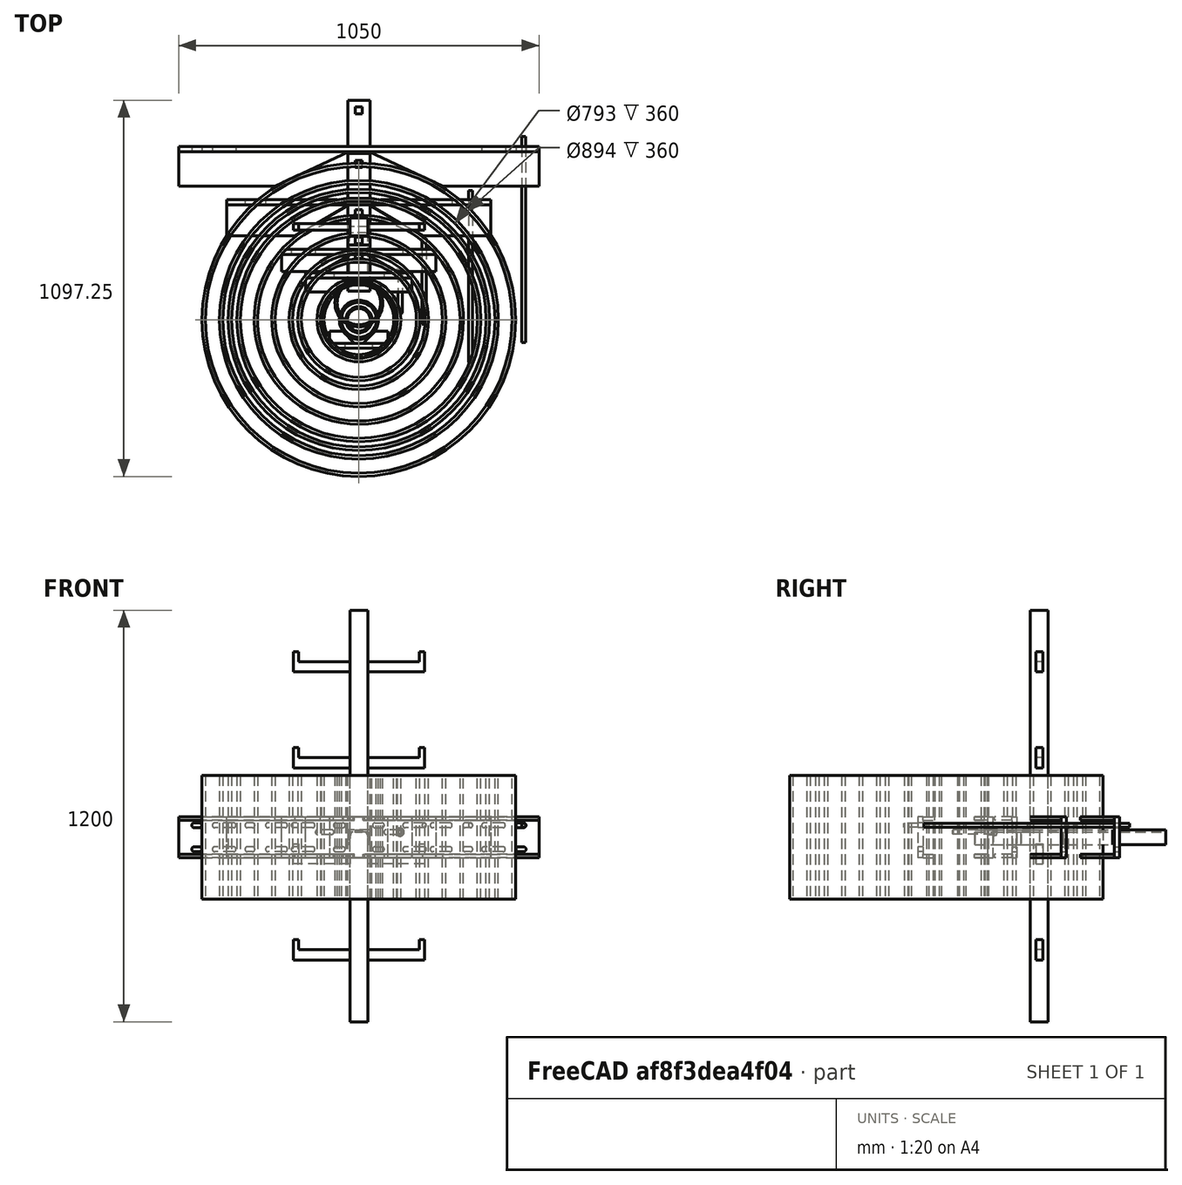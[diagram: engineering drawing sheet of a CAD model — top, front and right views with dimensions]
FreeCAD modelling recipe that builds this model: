
FCSTD DOCUMENT  (FreeCAD 0.21R33694 (Git))
Label: ladder_clamp
License: All rights reserved
LicenseURL: http://en.wikipedia.org/wiki/All_rights_reserved
objects: TechDraw::DrawViewDimension×53, Sketcher::SketchObject×26, Part::Extrusion×25, Part::FeaturePython×17, Part::Feature×15, Part::Cut×12, TechDraw::DrawProjGroupItem×12, App::DocumentObjectGroup×5, TechDraw::DrawSVGTemplate×4, TechDraw::DrawProjGroup×4, TechDraw::DrawViewBalloon×4, TechDraw::DrawViewAnnotation×4, TechDraw::DrawPage×4, Part::Cylinder×3, Fem::ConstraintForce×2, Part::MultiFuse×1, Fem::FemMeshObjectPython×1, Fem::FemSolverObjectPython×1, App::MaterialObjectPython×1, Fem::ConstraintFixed×1, +1 more types
note: 99 computed .brp shape members not serialized (recipe doc carries the construction recipe); baked Part::Feature solids carry a one-line shape summary decoded from their .brp

FEATURE [Part::Feature] BOLTS_part  label="Circular hollow profile 76.1/5.0 l=360.0"
  Placement = pos=(0,0,-120) rot=(0,0,1;0rad)
  shape: bbox 76.1 x 76.1 x 360 mm, 4 faces (baked)
FEATURE [Part::Feature] BOLTS_part001  label="Circular hollow profile 114.3/6.3 l=360.0"
  Placement = pos=(0,0,-120) rot=(0,0,1;0rad)
  shape: bbox 114.3 x 114.3 x 360 mm, 4 faces (baked)
FEATURE [Part::Feature] BOLTS_part002  label="Circular hollow profile 139.7/6.3 l=360.0"
  Placement = pos=(0,49,-120) rot=(0,0,1;0rad)
  shape: bbox 139.7 x 139.7 x 360 mm, 4 faces (baked)
FEATURE [Part::Feature] BOLTS_part003  label="Circular hollow profile 219.1/8.0 l=360.0"
  Placement = pos=(0,0,-120) rot=(0,0,1;0rad)
  shape: bbox 219.1 x 219.1 x 360 mm, 4 faces (baked)
FEATURE [Part::Feature] BOLTS_part004  label="Circular hollow profile 244.5/10.0 l=360.0"
  Placement = pos=(0,0,-120) rot=(0,0,1;0rad)
  shape: bbox 244.5 x 244.5 x 360 mm, 4 faces (baked)
FEATURE [Part::Feature] BOLTS_part005  label="Circular hollow profile 355.6/10.0 l=360.0"
  Placement = pos=(0,0,-120) rot=(0,0,1;0rad)
  shape: bbox 355.6 x 355.6 x 360 mm, 4 faces (baked)
FEATURE [Part::Feature] BOLTS_part006  label="Circular hollow profile 406.4/10.0 l=360.0"
  Placement = pos=(0,0,-120) rot=(0,0,1;0rad)
  shape: bbox 406.4 x 406.4 x 360 mm, 4 faces (baked)
FEATURE [Part::Feature] BOLTS_part007  label="Circular hollow profile 610.0/10.0 l=360.0"
  Placement = pos=(0,0,-120) rot=(0,0,1;0rad)
  shape: bbox 610 x 610 x 360 mm, 4 faces (baked)
FEATURE [Part::Feature] BOLTS_part008  label="Circular hollow profile 914.0/10.0 l=360.0"
  Placement = pos=(0,0,-120) rot=(0,0,1;0rad)
  shape: bbox 914 x 914 x 360 mm, 4 faces (baked)
FEATURE [Sketcher::SketchObject] Sketch
  FullyConstrained = true
  sketch-geometry (10):
    g0: Circle CenterX=0 CenterY=0 CenterZ=0 NormalX=0 NormalY=0 NormalZ=1 AngleXU=0 Radius=57.15
    g1: LineSegment StartX=-47.5 StartY=33.3223 StartZ=0 EndX=-12.5 EndY=68.3223 EndZ=0
    g2: LineSegment StartX=12.5 StartY=68.3223 StartZ=0 EndX=47.5 EndY=33.3223 EndZ=0
    g3: LineSegment StartX=-12.5 StartY=68.3223 StartZ=0 EndX=12.5 EndY=68.3223 EndZ=0
    g4: LineSegment StartX=47.5 StartY=33.3223 StartZ=0 EndX=85 EndY=33.3223 EndZ=0
    g5: LineSegment StartX=85 StartY=33.3223 StartZ=0 EndX=85 EndY=68.3223 EndZ=0
    g6: LineSegment StartX=85 StartY=68.3223 StartZ=0 EndX=12.5 EndY=68.3223 EndZ=0
    g7: LineSegment StartX=-12.5 StartY=68.3223 StartZ=0 EndX=-85 EndY=68.3223 EndZ=0
    g8: LineSegment StartX=-85 StartY=68.3223 StartZ=0 EndX=-85 EndY=33.3223 EndZ=0
    g9: LineSegment StartX=-85 StartY=33.3223 StartZ=0 EndX=-47.5 EndY=33.3223 EndZ=0
  constraints (26):
    c: Coincident(g0,g-1)
    c: Tangent(g1,g0)
    c: Symmetric(g1,g2,g-2)
    c: Symmetric(g1,g2,g-2)
    c: Coincident(g3,g1)
    c: Coincident(g3,g2)
    c: Angle(g-1,g1) = 0.785398
    c: Coincident(g2,g4)
    c: Horizontal(g4)
    c: Coincident(g4,g5)
    c: Vertical(g5)
    c: Coincident(g5,g6)
    c: Coincident(g6,g2)
    c: Horizontal(g6)
    c: Coincident(g1,g7)
    c: Horizontal(g7)
    c: Coincident(g7,g8)
    c: Vertical(g8)
    c: Coincident(g8,g9)
    c: Coincident(g9,g1)
    c: Horizontal(g9)
    c: DistanceY(g5,g5) = 35
    c: Equal(g6,g7)
    c: DistanceX(g6,g6) = 72.5
    c: DistanceX(g7,g5) = 170
    c: Diameter(g0) = 114.3
FEATURE [Part::Extrusion] Extrude  label="Eckblech"
  Base = -> Sketch
  Dir = (0,0,1)
  DirMode = 2
  FaceMakerClass = Part::FaceMakerBullseye
  LengthFwd = 10
  LengthRev = 0
  Solid = true
  Symmetric = false
FEATURE [Part::FeaturePython] Clone  label="Eckblech001"  # Draft clone (typed FeaturePython)
  AttacherType = Attacher::AttachEngine3D
  Fuse = false
  Objects = -> [Extrude]
  Placement = pos=(0,0,110) rot=(0,0,1;0rad)
  Scale = (1,1,1)
FEATURE [Sketcher::SketchObject] Sketch001
  ExternalGeometry = -> [Clone,Extrude]
  FullyConstrained = true
  MapMode = 5
  Placement = pos=(0,68.3223,0) rot=(0,0.707107,0.707107;3.14159rad)
  Support = -> [Extrude]
  sketch-geometry (4):
    g0: LineSegment StartX=-85 StartY=0 StartZ=0 EndX=85 EndY=0 EndZ=0
    g1: LineSegment StartX=85 StartY=0 StartZ=0 EndX=85 EndY=120 EndZ=0
    g2: LineSegment StartX=85 StartY=120 StartZ=0 EndX=-85 EndY=120 EndZ=0
    g3: LineSegment StartX=-85 StartY=120 StartZ=0 EndX=-85 EndY=0 EndZ=0
  constraints (10):
    c: Coincident(g0,g1)
    c: Coincident(g1,g2)
    c: Coincident(g2,g3)
    c: Coincident(g3,g0)
    c: Horizontal(g0)
    c: Horizontal(g2)
    c: Vertical(g1)
    c: Vertical(g3)
    c: Coincident(g0,g-4)
    c: Coincident(g1,g-3)
FEATURE [Part::Extrusion] Extrude001  label="Extrude002"
  Base = -> Sketch001
  Dir = (0,1,-2e-16)
  DirMode = 2
  FaceMakerClass = Part::FaceMakerBullseye
  LengthFwd = 15
  LengthRev = 0
  Solid = true
  Symmetric = false
FEATURE [Sketcher::SketchObject] Sketch002
  ExternalGeometry = -> [Extrude001]
  FullyConstrained = true
  MapMode = 5
  Placement = pos=(0,83.3223,-2e-14) rot=(0,0.707107,0.707107;3.14159rad)
  Support = -> [Extrude001]
  sketch-geometry (13):
    g0: LineSegment StartX=-32.5 StartY=39 StartZ=0 EndX=-32.5 EndY=81 EndZ=0
    g1: LineSegment StartX=-32.5 StartY=81 StartZ=0 EndX=32.5 EndY=81 EndZ=0
    g2: LineSegment StartX=32.5 StartY=81 StartZ=0 EndX=32.5 EndY=39 EndZ=0
    g3: LineSegment StartX=-32.5 StartY=81 StartZ=0 EndX=-85 EndY=120 EndZ=0
    g4: LineSegment StartX=32.5 StartY=81 StartZ=0 EndX=85 EndY=120 EndZ=0
    g5: LineSegment StartX=-16.5 StartY=75.5 StartZ=0 EndX=16.5 EndY=75.5 EndZ=0
    g6: LineSegment StartX=23.89 StartY=69.2796 StartZ=0 EndX=28.5586 EndY=42.3175 EndZ=0
    g7: LineSegment StartX=-23.89 StartY=69.2796 StartZ=0 EndX=-28.5586 EndY=42.3175 EndZ=0
    g8: ArcOfCircle CenterX=32.5 CenterY=43 CenterZ=0 NormalX=0 NormalY=0 NormalZ=1 AngleXU=0 Radius=4 StartAngle=3.31305 EndAngle=4.71239
    g9: ArcOfCircle CenterX=16.5 CenterY=68 CenterZ=0 NormalX=0 NormalY=0 NormalZ=1 AngleXU=0 Radius=7.5 StartAngle=0.171455 EndAngle=1.5708
    g10: ArcOfCircle CenterX=-32.5 CenterY=43 CenterZ=0 NormalX=0 NormalY=0 NormalZ=1 AngleXU=0 Radius=4 StartAngle=4.71239 EndAngle=6.11173
    g11: ArcOfCircle CenterX=-16.5 CenterY=68 CenterZ=0 NormalX=0 NormalY=0 NormalZ=1 AngleXU=0 Radius=7.5 StartAngle=1.5708 EndAngle=2.97014
    g12: LineSegment StartX=-85 StartY=1.42e-14 StartZ=0 EndX=-32.5 EndY=39 EndZ=0
  constraints (35):
    c: Vertical(g0)
    c: Coincident(g0,g1)
    c: Horizontal(g1)
    c: Coincident(g1,g2)
    c: Vertical(g2)
    c: Coincident(g3,g0)
    c: Coincident(g4,g1)
    c: Coincident(g3,g-4)
    c: Coincident(g4,g-3)
    c: Equal(g3,g4)
    c: DistanceX(g1,g1) = 65
    c: DistanceY(g0,g0) = 42
    c: Equal(g0,g2)
    c: PointOnObject(g8,g2)
    c: Coincident(g8,g2)
    c: Coincident(g9,g5)
    c: Vertical(g9,g5)
    c: Tangent(g6,g9) = 1.5708
    c: Tangent(g8,g6) = -1.5708
    c: Symmetric(g5,g5,g-2)
    c: DistanceY(g5,g1) = 5.5
    c: Radius(g9) = 7.5
    c: Radius(g8) = 4
    c: DistanceX(g5,g5) = 33
    c: PointOnObject(g10,g0)
    c: Coincident(g10,g0)
    c: Coincident(g11,g5)
    c: Vertical(g11,g5)
    c: Equal(g9,g11)
    c: Tangent(g11,g7) = -1.5708
    c: Equal(g8,g10)
    c: Tangent(g10,g7) = 1.5708
    c: Coincident(g12,g-4)
    c: Coincident(g12,g0)
    c: Equal(g3,g12)
FEATURE [Part::Extrusion] Extrude002  label="Extrude003"
  Base = -> Sketch002
  Dir = (0,1,-2e-16)
  DirMode = 2
  FaceMakerClass = Part::FaceMakerBullseye
  LengthFwd = 135
  LengthRev = 0
  Solid = true
  Symmetric = false
FEATURE [Sketcher::SketchObject] Sketch003
  ExternalGeometry = -> [Extrude002]
  FullyConstrained = true
  MapMode = 5
  Placement = pos=(0,1.78e-14,81) rot=(0,0,1;0rad)
  Support = -> [Extrude002]
  sketch-geometry (7):
    g0: LineSegment StartX=-10 StartY=198.322 StartZ=0 EndX=10 EndY=198.322 EndZ=0
    g1: LineSegment StartX=10 StartY=198.322 StartZ=0 EndX=10 EndY=178.322 EndZ=0
    g2: LineSegment StartX=10 StartY=178.322 StartZ=0 EndX=-10 EndY=178.322 EndZ=0
    g3: LineSegment StartX=-10 StartY=178.322 StartZ=0 EndX=-10 EndY=198.322 EndZ=0
    g4: LineSegment StartX=-10 StartY=198.322 StartZ=0 EndX=-32.5 EndY=218.322 EndZ=0
    g5: LineSegment StartX=10 StartY=198.322 StartZ=0 EndX=32.5 EndY=218.322 EndZ=0
    g6: LineSegment StartX=10 StartY=188.322 StartZ=0 EndX=32.5 EndY=188.322 EndZ=0
  constraints (19):
    c: Coincident(g0,g1)
    c: Coincident(g1,g2)
    c: Coincident(g2,g3)
    c: Coincident(g3,g0)
    c: Horizontal(g0)
    c: Horizontal(g2)
    c: Vertical(g1)
    c: Vertical(g3)
    c: DistanceX(g2,g2) = 20
    c: DistanceY(g1,g1) = 20
    c: Coincident(g4,g0)
    c: Coincident(g5,g0)
    c: Coincident(g4,g-3)
    c: Coincident(g5,g-3)
    c: Equal(g4,g5)
    c: PointOnObject(g6,g1)
    c: Vertical(g5,g6)
    c: Symmetric(g1,g0,g6)
    c: DistanceY(g6,g5) = 30
FEATURE [Part::Extrusion] Extrude003  label="Extrude004"
  Base = -> Sketch003
  Dir = (0,2e-16,1)
  DirMode = 2
  FaceMakerClass = Part::FaceMakerBullseye
  LengthFwd = 30
  LengthRev = 0
  Solid = true
  Symmetric = true
FEATURE [Part::Cut] Cut  label="U65"
  Base = -> Extrude002
  Refine = true
  Tool = -> Extrude003
FEATURE [Sketcher::SketchObject] Sketch004
  ExternalGeometry = -> [Clone,Extrude]
  FullyConstrained = true
  MapMode = 5
  Placement = pos=(0,68.3223,-1.64e-14) rot=(1,0,0;1.5708rad)
  Support = -> [Extrude001]
  sketch-geometry (19):
    g0: ArcOfCircle CenterX=-67 CenterY=95 CenterZ=0 NormalX=0 NormalY=0 NormalZ=1 AngleXU=0 Radius=7 StartAngle=1.5708 EndAngle=4.71239
    g1: ArcOfCircle CenterX=-47 CenterY=95 CenterZ=0 NormalX=0 NormalY=0 NormalZ=1 AngleXU=0 Radius=7 StartAngle=4.71239 EndAngle=7.85398
    g2: LineSegment StartX=-67 StartY=88 StartZ=0 EndX=-47 EndY=88 EndZ=0
    g3: LineSegment StartX=-67 StartY=102 StartZ=0 EndX=-47 EndY=102 EndZ=0
    g4: ArcOfCircle CenterX=47 CenterY=95 CenterZ=0 NormalX=0 NormalY=0 NormalZ=1 AngleXU=0 Radius=7 StartAngle=1.5708 EndAngle=4.71239
    g5: ArcOfCircle CenterX=67 CenterY=95 CenterZ=0 NormalX=0 NormalY=0 NormalZ=1 AngleXU=0 Radius=7 StartAngle=4.71239 EndAngle=7.85398
    g6: LineSegment StartX=47 StartY=88 StartZ=0 EndX=67 EndY=88 EndZ=0
    g7: LineSegment StartX=47 StartY=102 StartZ=0 EndX=67 EndY=102 EndZ=0
    g8: ArcOfCircle CenterX=-67 CenterY=25 CenterZ=0 NormalX=0 NormalY=0 NormalZ=1 AngleXU=0 Radius=7 StartAngle=1.5708 EndAngle=4.71239
    g9: ArcOfCircle CenterX=-47 CenterY=25 CenterZ=0 NormalX=0 NormalY=0 NormalZ=1 AngleXU=0 Radius=7 StartAngle=4.71239 EndAngle=7.85398
    g10: LineSegment StartX=-67 StartY=18 StartZ=0 EndX=-47 EndY=18 EndZ=0
    g11: LineSegment StartX=-67 StartY=32 StartZ=0 EndX=-47 EndY=32 EndZ=0
    g12: ArcOfCircle CenterX=47 CenterY=25 CenterZ=0 NormalX=0 NormalY=0 NormalZ=1 AngleXU=0 Radius=7 StartAngle=1.5708 EndAngle=4.71239
    g13: ArcOfCircle CenterX=67 CenterY=25 CenterZ=0 NormalX=0 NormalY=0 NormalZ=1 AngleXU=0 Radius=7 StartAngle=4.71239 EndAngle=7.85398
    g14: LineSegment StartX=47 StartY=18 StartZ=0 EndX=67 EndY=18 EndZ=0
    g15: LineSegment StartX=47 StartY=32 StartZ=0 EndX=67 EndY=32 EndZ=0
    g16: LineSegment StartX=-85 StartY=110 StartZ=0 EndX=-67 EndY=95 EndZ=0
    g17: LineSegment StartX=85 StartY=110 StartZ=0 EndX=67 EndY=95 EndZ=0
    g18: LineSegment StartX=-85 StartY=10 StartZ=0 EndX=-67 EndY=25 EndZ=0
  constraints (44):
    c: Tangent(g0,g3) = 1.5708
    c: Tangent(g2,g1) = -1.5708
    c: Tangent(g3,g1) = 1.5708
    c: Equal(g0,g1)
    c: Tangent(g4,g7) = 1.5708
    c: Tangent(g4,g6) = -1.5708
    c: Tangent(g6,g5) = -1.5708
    c: Tangent(g7,g5) = 1.5708
    c: Horizontal(g6)
    c: Equal(g4,g5)
    c: Tangent(g8,g11) = 1.5708
    c: Tangent(g8,g10) = -1.5708
    c: Tangent(g10,g9) = -1.5708
    c: Tangent(g11,g9) = 1.5708
    c: Horizontal(g10)
    c: Equal(g8,g9)
    c: Tangent(g12,g15) = 1.5708
    c: Tangent(g12,g14) = -1.5708
    c: Tangent(g14,g13) = -1.5708
    c: Tangent(g15,g13) = 1.5708
    c: Horizontal(g14)
    c: Equal(g12,g13)
    c: Symmetric(g1,g4,g-2)
    c: Symmetric(g9,g12,g-2)
    c: Vertical(g1,g9)
    c: Equal(g9,g1)
    c: Equal(g1,g4)
    c: Equal(g4,g12)
    c: Equal(g3,g11)
    c: Equal(g11,g7)
    c: Equal(g7,g15)
    c: Diameter(g0) = 14
    c: DistanceX(g3,g3) = 20
    c: Coincident(g16,g-4)
    c: Coincident(g16,g0)
    c: Coincident(g17,g-3)
    c: Coincident(g17,g5)
    c: DistanceY(g8,g0) = 70
    c: Tangent(g0,g2) = -1.5708
    c: DistanceX(g1,g4) = 94
    c: Horizontal(g2)
    c: Coincident(g18,g-6)
    c: Coincident(g18,g8)
    c: Equal(g16,g18)
FEATURE [Part::Extrusion] Extrude004  label="Extrude005"
  Base = -> Sketch004
  Dir = (0,1,0)
  DirMode = 0
  FaceMakerClass = Part::FaceMakerBullseye
  LengthFwd = 50
  LengthRev = 0
  Solid = true
  Symmetric = true
FEATURE [Part::Cut] Cut001
  Base = -> Extrude001
  Refine = true
  Tool = -> Extrude004
FEATURE [Part::FeaturePython] BooleanFragments  # WARN: FeaturePython — macro-defined, semantics opaque (R4)
  Mode = 0
  Objects = -> [Extrude,Clone,Cut001]
  Tolerance = 0
FEATURE [Part::FeaturePython] Clone001  label="BooleanFragments001"  # Draft clone (typed FeaturePython)
  AttacherType = Attacher::AttachEngine3D
  Fuse = false
  Objects = -> [BooleanFragments]
  Placement = pos=(0,0,0) rot=(0,0,1;3.14159rad)
  Scale = (1,1,1)
FEATURE [Sketcher::SketchObject] Sketch005  label="Basis"
  FullyConstrained = true
  sketch-geometry (10):
    g0: Circle CenterX=0 CenterY=0 CenterZ=0 NormalX=0 NormalY=0 NormalZ=1 AngleXU=0 Radius=57.15
    g1: LineSegment StartX=-47.5 StartY=33.3223 StartZ=0 EndX=-12.5 EndY=68.3223 EndZ=0
    g2: LineSegment StartX=12.5 StartY=68.3223 StartZ=0 EndX=47.5 EndY=33.3223 EndZ=0
    g3: LineSegment StartX=-12.5 StartY=68.3223 StartZ=0 EndX=12.5 EndY=68.3223 EndZ=0
    g4: LineSegment StartX=47.5 StartY=33.3223 StartZ=0 EndX=85 EndY=33.3223 EndZ=0
    g5: LineSegment StartX=85 StartY=33.3223 StartZ=0 EndX=85 EndY=68.3223 EndZ=0
    g6: LineSegment StartX=85 StartY=68.3223 StartZ=0 EndX=12.5 EndY=68.3223 EndZ=0
    g7: LineSegment StartX=-12.5 StartY=68.3223 StartZ=0 EndX=-85 EndY=68.3223 EndZ=0
    g8: LineSegment StartX=-85 StartY=68.3223 StartZ=0 EndX=-85 EndY=33.3223 EndZ=0
    g9: LineSegment StartX=-85 StartY=33.3223 StartZ=0 EndX=-47.5 EndY=33.3223 EndZ=0
  constraints (26):
    c: Coincident(g0,g-1)
    c: Tangent(g1,g0)
    c: Symmetric(g1,g2,g-2)
    c: Symmetric(g1,g2,g-2)
    c: Coincident(g3,g1)
    c: Coincident(g3,g2)
    c: Angle(g-1,g1) = 0.785398
    c: Coincident(g2,g4)
    c: Horizontal(g4)
    c: Coincident(g4,g5)
    c: Vertical(g5)
    c: Coincident(g5,g6)
    c: Coincident(g6,g2)
    c: Horizontal(g6)
    c: Coincident(g1,g7)
    c: Horizontal(g7)
    c: Coincident(g7,g8)
    c: Vertical(g8)
    c: Coincident(g8,g9)
    c: Coincident(g9,g1)
    c: Horizontal(g9)
    c: DistanceY(g5,g5) = 35
    c: Equal(g6,g7)
    c: DistanceX(g6,g6) = 72.5
    c: DistanceX(g7,g5) = 170
    c: Diameter(g0) = 114.3
FEATURE [App::DocumentObjectGroup] Group001  label="R76_114"
  Group = -> [Cut,BooleanFragments,Clone001,BOLTS_part,BOLTS_part001,Sketch005]
FEATURE [TechDraw::DrawSVGTemplate] Template
  EditableTexts = AUTHOR_NAME=Thomas Schrader,DN=1,DRAWING_TITLE=Leiterhalterung,FC-DATE=06.05.2021,FC-SC=1:2,FC-SH=X / Y,FC-SI=A3,FreeCAD_DRAWING=Material: Stahl S235,+5 more (map truncated)
  Height = 297
  Orientation = 1
  Width = 420
FEATURE [TechDraw::DrawProjGroupItem] ProjItem  label="Front"
  CoarseView = false
  Direction = (0,1,0)
  Focus = 100
  HardHidden = false
  IsoCount = 0
  IsoHidden = false
  IsoVisible = false
  LockPosition = true
  Perspective = false
  Rotation = 0
  RotationVector = (-1,0,0)
  Scale = 0.5
  ScaleType = 2
  ScrubCount = 0
  SeamHidden = false
  SeamVisible = true
  SmoothHidden = false
  SmoothVisible = true
  Source = -> [Cut,BooleanFragments]
  Type = 0
  X = 0
  XDirection = (-1,0,0)
  Y = 0
FEATURE [TechDraw::DrawProjGroupItem] ProjItem001  label="Left"
  CoarseView = false
  Direction = (1,1e-16,0)
  Focus = 100
  HardHidden = true
  IsoCount = 0
  IsoHidden = false
  IsoVisible = false
  LockPosition = false
  Perspective = false
  Rotation = 0
  RotationVector = (1,0,0)
  Scale = 0.2
  ScaleType = 2
  ScrubCount = 0
  SeamHidden = false
  SeamVisible = true
  SmoothHidden = false
  SmoothVisible = true
  Source = -> [Cut,BooleanFragments]
  Type = 1
  X = 103.75
  XDirection = (-1e-16,1,0)
  Y = 0
FEATURE [TechDraw::DrawProjGroupItem] ProjItem002  label="Top"
  CoarseView = false
  Direction = (0,0,1)
  Focus = 100
  HardHidden = true
  IsoCount = 0
  IsoHidden = false
  IsoVisible = false
  LockPosition = false
  Perspective = false
  Rotation = 0
  RotationVector = (1,0,0)
  Scale = 0.2
  ScaleType = 2
  ScrubCount = 0
  SeamHidden = false
  SeamVisible = true
  SmoothHidden = false
  SmoothVisible = true
  Source = -> [Cut,BooleanFragments]
  Type = 4
  X = 0
  XDirection = (-1,0,0)
  Y = -91.25
FEATURE [TechDraw::DrawProjGroup] ProjGroup
  Anchor = -> ProjItem
  AutoDistribute = true
  LockPosition = false
  ProjectionType = 0
  Rotation = 0
  Scale = 0.5
  ScaleType = 2
  Source = -> [Cut,BooleanFragments]
  Views = -> [ProjItem,ProjItem001,ProjItem002]
  X = 116.09
  Y = 219.887
  spacingX = 15
  spacingY = 15
FEATURE [TechDraw::DrawViewDimension] Dimension
  AngleOverride = false
  Arbitrary = false
  ArbitraryTolerances = false
  EqualTolerance = true
  ExtensionAngle = 0
  FormatSpec = %.1f
  FormatSpecOverTolerance = %+.1f
  FormatSpecUnderTolerance = %+.1f
  Inverted = false
  LineAngle = 0
  LockPosition = false
  MeasureType = 1
  OverTolerance = 0
  References2D = -> [ProjItem002]
  Rotation = 0
  Scale = 0.2
  ScaleType = 2
  TheoreticalExact = false
  Type = 2
  UnderTolerance = 0
  X = -71.0566
  Y = 37.5
FEATURE [TechDraw::DrawViewDimension] Dimension001
  AngleOverride = false
  Arbitrary = false
  ArbitraryTolerances = false
  EqualTolerance = true
  ExtensionAngle = 0
  FormatSpec = %.1f
  FormatSpecOverTolerance = %+.1f
  FormatSpecUnderTolerance = %+.1f
  Inverted = false
  LineAngle = 0
  LockPosition = false
  MeasureType = 1
  OverTolerance = 0
  References2D = -> [ProjItem002]
  Rotation = 0
  Scale = 0.2
  ScaleType = 2
  TheoreticalExact = false
  Type = 2
  UnderTolerance = 0
  X = -64.7644
  Y = 11.2057
FEATURE [TechDraw::DrawViewDimension] Dimension002
  AngleOverride = false
  Arbitrary = false
  ArbitraryTolerances = false
  EqualTolerance = true
  ExtensionAngle = 0
  FormatSpec = %.1f
  FormatSpecOverTolerance = %+.1f
  FormatSpecUnderTolerance = %+.1f
  Inverted = false
  LineAngle = 0
  LockPosition = false
  MeasureType = 1
  OverTolerance = 0
  References2D = -> [ProjItem]
  Rotation = 0
  Scale = 0.2
  ScaleType = 2
  TheoreticalExact = false
  Type = 1
  UnderTolerance = 0
  X = -0.318123
  Y = 46.2243
FEATURE [TechDraw::DrawViewDimension] Dimension003
  AngleOverride = false
  Arbitrary = false
  ArbitraryTolerances = false
  EqualTolerance = true
  ExtensionAngle = 0
  FormatSpec = %.1f
  FormatSpecOverTolerance = %+.1f
  FormatSpecUnderTolerance = %+.1f
  Inverted = false
  LineAngle = 0
  LockPosition = false
  MeasureType = 1
  OverTolerance = 0
  References2D = -> [ProjItem]
  Rotation = 0
  Scale = 0.2
  ScaleType = 2
  TheoreticalExact = false
  Type = 2
  UnderTolerance = 0
  X = -71.4492
  Y = 0.95437
FEATURE [TechDraw::DrawViewDimension] Dimension004
  AngleOverride = false
  Arbitrary = false
  ArbitraryTolerances = false
  EqualTolerance = true
  ExtensionAngle = 0
  FormatSpec = ⌀%.1f
  FormatSpecOverTolerance = %+.1f
  FormatSpecUnderTolerance = %+.1f
  Inverted = false
  LineAngle = 0
  LockPosition = false
  MeasureType = 1
  OverTolerance = 0
  References2D = -> [ProjItem]
  Rotation = 0
  Scale = 0.2
  ScaleType = 2
  TheoreticalExact = false
  Type = 5
  UnderTolerance = 0
  X = 49.0059
  Y = 14.3186
FEATURE [TechDraw::DrawViewDimension] Dimension005
  AngleOverride = false
  Arbitrary = false
  ArbitraryTolerances = false
  EqualTolerance = true
  ExtensionAngle = 0
  FormatSpec = %.1f
  FormatSpecOverTolerance = %+.1f
  FormatSpecUnderTolerance = %+.1f
  Inverted = false
  LineAngle = 0
  LockPosition = false
  MeasureType = 1
  OverTolerance = 0
  References2D = -> [ProjItem]
  Rotation = 0
  Scale = 0.2
  ScaleType = 2
  TheoreticalExact = false
  Type = 1
  UnderTolerance = 0
  X = -28.5
  Y = 7.01313
FEATURE [TechDraw::DrawViewDimension] Dimension006
  AngleOverride = false
  Arbitrary = false
  ArbitraryTolerances = false
  EqualTolerance = true
  ExtensionAngle = 0
  FormatSpec = %.1f
  FormatSpecOverTolerance = %+.1f
  FormatSpecUnderTolerance = %+.1f
  Inverted = false
  LineAngle = 0
  LockPosition = false
  MeasureType = 1
  OverTolerance = 0
  References2D = -> [ProjItem]
  Rotation = 0
  Scale = 0.2
  ScaleType = 2
  TheoreticalExact = false
  Type = 2
  UnderTolerance = 0
  X = -54.6754
  Y = 3.4284
FEATURE [TechDraw::DrawViewDimension] Dimension007
  AngleOverride = false
  Arbitrary = false
  ArbitraryTolerances = false
  EqualTolerance = true
  ExtensionAngle = 0
  FormatSpec = %.1f
  FormatSpecOverTolerance = %+.1f
  FormatSpecUnderTolerance = %+.1f
  Inverted = false
  LineAngle = 0
  LockPosition = false
  MeasureType = 1
  OverTolerance = 0
  References2D = -> [ProjItem]
  Rotation = 0
  Scale = 0.2
  ScaleType = 2
  TheoreticalExact = false
  Type = 1
  UnderTolerance = 0
  X = -0.403341
  Y = -37.2637
FEATURE [TechDraw::DrawViewDimension] Dimension008
  AngleOverride = false
  Arbitrary = false
  ArbitraryTolerances = false
  EqualTolerance = true
  ExtensionAngle = 0
  FormatSpec = %.1f
  FormatSpecOverTolerance = %+.1f
  FormatSpecUnderTolerance = %+.1f
  Inverted = false
  LineAngle = 0
  LockPosition = false
  MeasureType = 1
  OverTolerance = 0
  References2D = -> [ProjItem002]
  Rotation = 0
  Scale = 0.2
  ScaleType = 2
  TheoreticalExact = false
  Type = 1
  UnderTolerance = 0
  X = 32.8723
  Y = -34.6868
FEATURE [TechDraw::DrawViewDimension] Dimension009
  AngleOverride = false
  Arbitrary = false
  ArbitraryTolerances = false
  EqualTolerance = true
  ExtensionAngle = 0
  FormatSpec = %.1f
  FormatSpecOverTolerance = %+.1f
  FormatSpecUnderTolerance = %+.1f
  Inverted = false
  LineAngle = 0
  LockPosition = false
  MeasureType = 1
  OverTolerance = 0
  References2D = -> [ProjItem002]
  Rotation = 0
  Scale = 0.2
  ScaleType = 2
  TheoreticalExact = false
  Type = 2
  UnderTolerance = 0
  X = 19.5011
  Y = -16.5424
FEATURE [TechDraw::DrawViewDimension] Dimension010
  AngleOverride = false
  Arbitrary = false
  ArbitraryTolerances = false
  EqualTolerance = true
  ExtensionAngle = 0
  FormatSpec = %.1f
  FormatSpecOverTolerance = %+.1f
  FormatSpecUnderTolerance = %+.1f
  Inverted = false
  LineAngle = 0
  LockPosition = false
  MeasureType = 1
  OverTolerance = 0
  References2D = -> [ProjItem002]
  Rotation = 0
  Scale = 0.2
  ScaleType = 2
  TheoreticalExact = false
  Type = 2
  UnderTolerance = 0
  X = -50.5722
  Y = 0.025058
FEATURE [TechDraw::DrawViewDimension] Dimension011
  AngleOverride = false
  Arbitrary = false
  ArbitraryTolerances = false
  EqualTolerance = true
  ExtensionAngle = 0
  FormatSpec = %.1f
  FormatSpecOverTolerance = %+.1f
  FormatSpecUnderTolerance = %+.1f
  Inverted = false
  LineAngle = 0
  LockPosition = false
  MeasureType = 1
  OverTolerance = 0
  References2D = -> [ProjItem001]
  Rotation = 0
  Scale = 0.2
  ScaleType = 2
  TheoreticalExact = false
  Type = 1
  UnderTolerance = 0
  X = 12.5684
  Y = 23.4751
FEATURE [TechDraw::DrawViewBalloon] Balloon
  BubbleShape = 0
  EndType = 0
  EndTypeScale = 1
  KinkLength = 5
  LockPosition = false
  OriginX = 82.506
  OriginY = -1.18058
  Rotation = 0
  Scale = 0.2
  ScaleType = 2
  ShapeScale = 1
  SourceView = -> ProjItem001
  Text = 1
  TextWrapLen = -1
  X = 122.506
  Y = 38.8194
FEATURE [TechDraw::DrawViewAnnotation] Annotation
  Font = Arial
  LineSpace = 80
  LockPosition = false
  MaxWidth = -1
  Rotation = 0
  Scale = 0.2
  ScaleType = 2
  Text = U-65
  TextSize = 5
  TextStyle = 0
  X = 299.213
  Y = 237.713
FEATURE [TechDraw::DrawPage] Page  label="Page_R76_R114"
  KeepUpdated = true
  NextBalloonIndex = 2
  ProjectionType = 0
  Template = -> Template
  Views = -> [ProjGroup,Dimension,Dimension001,Dimension002,Dimension003,Dimension004,Dimension005,Dimension006,Dimension007,Dimension008,Dimension009,Dimension010,Dimension011,Balloon,Annotation]
FEATURE [Sketcher::SketchObject] Sketch007
  FullyConstrained = true
  sketch-geometry (10):
    g0: Circle CenterX=0 CenterY=0 CenterZ=0 NormalX=0 NormalY=0 NormalZ=1 AngleXU=0 Radius=109.55
    g1: LineSegment StartX=-74.6259 StartY=81.4822 StartZ=0 EndX=-17.5 EndY=121.482 EndZ=0
    g2: LineSegment StartX=17.5 StartY=121.482 StartZ=0 EndX=74.6259 EndY=81.4822 EndZ=0
    g3: LineSegment StartX=-17.5 StartY=121.482 StartZ=0 EndX=17.5 EndY=121.482 EndZ=0
    g4: LineSegment StartX=74.6259 StartY=81.4822 StartZ=0 EndX=155 EndY=81.4822 EndZ=0
    g5: LineSegment StartX=155 StartY=81.4822 StartZ=0 EndX=155 EndY=121.482 EndZ=0
    g6: LineSegment StartX=155 StartY=121.482 StartZ=0 EndX=17.5 EndY=121.482 EndZ=0
    g7: LineSegment StartX=-17.5 StartY=121.482 StartZ=0 EndX=-155 EndY=121.482 EndZ=0
    g8: LineSegment StartX=-155 StartY=121.482 StartZ=0 EndX=-155 EndY=81.4822 EndZ=0
    g9: LineSegment StartX=-155 StartY=81.4822 StartZ=0 EndX=-74.6259 EndY=81.4822 EndZ=0
  constraints (26):
    c: Coincident(g0,g-1)
    c: Tangent(g1,g0)
    c: Symmetric(g1,g2,g-2)
    c: Symmetric(g1,g2,g-2)
    c: Coincident(g3,g1)
    c: Coincident(g3,g2)
    c: Coincident(g2,g4)
    c: Horizontal(g4)
    c: Coincident(g4,g5)
    c: Vertical(g5)
    c: Coincident(g5,g6)
    c: Coincident(g6,g2)
    c: Horizontal(g6)
    c: Coincident(g1,g7)
    c: Horizontal(g7)
    c: Coincident(g7,g8)
    c: Vertical(g8)
    c: Coincident(g8,g9)
    c: Coincident(g9,g1)
    c: Horizontal(g9)
    c: DistanceY(g5,g5) = 40
    c: Equal(g6,g7)
    c: Diameter(g0) = 219.1
    c: DistanceX(g1,g2) = 35
    c: Angle(g-1,g1) = 0.610865
    c: DistanceX(g7,g5) = 310
FEATURE [Part::Extrusion] Extrude005  label="Eckblech002"
  Base = -> Sketch007
  Dir = (0,0,1)
  DirMode = 2
  FaceMakerClass = Part::FaceMakerBullseye
  LengthFwd = 10
  LengthRev = 0
  Solid = true
  Symmetric = false
FEATURE [Part::FeaturePython] Clone004  label="Eckblech003"  # Draft clone (typed FeaturePython)
  AttacherType = Attacher::AttachEngine3D
  Fuse = false
  Objects = -> [Extrude005]
  Placement = pos=(0,0,110) rot=(0,0,1;0rad)
  Scale = (1,1,1)
FEATURE [Sketcher::SketchObject] Sketch008
  ExternalGeometry = -> [Clone004,Extrude005]
  FullyConstrained = true
  MapMode = 5
  Placement = pos=(0,121.482,0) rot=(0,0.707107,0.707107;3.14159rad)
  Support = -> [Extrude005]
  sketch-geometry (4):
    g0: LineSegment StartX=-155 StartY=0 StartZ=0 EndX=155 EndY=0 EndZ=0
    g1: LineSegment StartX=155 StartY=0 StartZ=0 EndX=155 EndY=120 EndZ=0
    g2: LineSegment StartX=155 StartY=120 StartZ=0 EndX=-155 EndY=120 EndZ=0
    g3: LineSegment StartX=-155 StartY=120 StartZ=0 EndX=-155 EndY=0 EndZ=0
  constraints (10):
    c: Coincident(g0,g1)
    c: Coincident(g1,g2)
    c: Coincident(g2,g3)
    c: Coincident(g3,g0)
    c: Horizontal(g0)
    c: Horizontal(g2)
    c: Vertical(g1)
    c: Vertical(g3)
    c: Coincident(g0,g-4)
    c: Coincident(g1,g-3)
FEATURE [Part::Extrusion] Extrude006
  Base = -> Sketch008
  Dir = (0,1,-2e-16)
  DirMode = 2
  FaceMakerClass = Part::FaceMakerBullseye
  LengthFwd = 15
  LengthRev = 0
  Solid = true
  Symmetric = false
FEATURE [Sketcher::SketchObject] Sketch009
  ExternalGeometry = -> [Extrude006]
  FullyConstrained = true
  MapMode = 5
  Placement = pos=(0,136.482,-3.28e-14) rot=(0,0.707107,0.707107;3.14159rad)
  Support = -> [Extrude006]
  sketch-geometry (11):
    g0: LineSegment StartX=-32.5 StartY=39 StartZ=0 EndX=-32.5 EndY=81 EndZ=0
    g1: LineSegment StartX=-32.5 StartY=81 StartZ=0 EndX=32.5 EndY=81 EndZ=0
    g2: LineSegment StartX=32.5 StartY=81 StartZ=0 EndX=32.5 EndY=39 EndZ=0
    g3: LineSegment StartX=-32.5 StartY=81 StartZ=0 EndX=-155 EndY=120 EndZ=0
    g4: LineSegment StartX=32.5 StartY=81 StartZ=0 EndX=155 EndY=120 EndZ=0
    g5: LineSegment StartX=-26.5 StartY=75.5 StartZ=0 EndX=26.5 EndY=75.5 EndZ=0
    g6: LineSegment StartX=26.5 StartY=75.5 StartZ=0 EndX=26.5 EndY=39 EndZ=0
    g7: LineSegment StartX=-26.5 StartY=75.5 StartZ=0 EndX=-26.5 EndY=39 EndZ=0
    g8: LineSegment StartX=-155 StartY=2.84e-14 StartZ=0 EndX=-32.5 EndY=39 EndZ=0
    g9: LineSegment StartX=-32.5 StartY=39 StartZ=0 EndX=-26.5 EndY=39 EndZ=0
    g10: LineSegment StartX=26.5 StartY=39 StartZ=0 EndX=32.5 EndY=39 EndZ=0
  constraints (29):
    c: Vertical(g0)
    c: Coincident(g0,g1)
    c: Horizontal(g1)
    c: Coincident(g1,g2)
    c: Vertical(g2)
    c: Coincident(g3,g0)
    c: Coincident(g4,g1)
    c: Coincident(g3,g-4)
    c: Coincident(g4,g-3)
    c: Equal(g3,g4)
    c: DistanceX(g1,g1) = 65
    c: DistanceY(g0,g0) = 42
    c: Equal(g0,g2)
    c: Symmetric(g5,g5,g-2)
    c: DistanceY(g5,g1) = 5.5
    c: Coincident(g8,g-4)
    c: Coincident(g8,g0)
    c: Equal(g3,g8)
    c: Vertical(g7)
    c: Vertical(g6)
    c: Coincident(g7,g5)
    c: Coincident(g5,g6)
    c: Coincident(g9,g0)
    c: Coincident(g9,g7)
    c: Horizontal(g9)
    c: Coincident(g10,g6)
    c: Coincident(g10,g2)
    c: Horizontal(g10)
    c: DistanceX(g10,g10) = 6
FEATURE [Part::Extrusion] Extrude007
  Base = -> Sketch009
  Dir = (0,1,-2e-16)
  DirMode = 2
  FaceMakerClass = Part::FaceMakerBullseye
  LengthFwd = 135
  LengthRev = 0
  Solid = true
  Symmetric = false
FEATURE [Sketcher::SketchObject] Sketch006
  ExternalGeometry = -> [Extrude007]
  FullyConstrained = true
  MapMode = 5
  Placement = pos=(0,8.6e-15,39) rot=(1,0,0;3.14159rad)
  Support = -> [Extrude007]
  sketch-geometry (4):
    g0: LineSegment StartX=-10 StartY=-221.482 StartZ=0 EndX=10 EndY=-221.482 EndZ=0
    g1: LineSegment StartX=10 StartY=-221.482 StartZ=0 EndX=10 EndY=-241.482 EndZ=0
    g2: LineSegment StartX=10 StartY=-241.482 StartZ=0 EndX=-10 EndY=-241.482 EndZ=0
    g3: LineSegment StartX=-10 StartY=-241.482 StartZ=0 EndX=-10 EndY=-221.482 EndZ=0
  constraints (11):
    c: Coincident(g0,g1)
    c: Coincident(g1,g2)
    c: Coincident(g2,g3)
    c: Coincident(g3,g0)
    c: Horizontal(g0)
    c: Vertical(g1)
    c: Vertical(g3)
    c: DistanceX(g2,g2) = 20
    c: DistanceY(g1,g1) = 20
    c: Symmetric(g2,g1,g-2)
    c: DistanceY(g-3,g1) = 30
FEATURE [Sketcher::SketchObject] Sketch010
  ExternalGeometry = -> [Clone004,Extrude005]
  FullyConstrained = true
  MapMode = 5
  Placement = pos=(0,121.482,-2.92e-14) rot=(1,0,0;1.5708rad)
  Support = -> [Extrude006]
  sketch-geometry (10):
    g0: ArcOfCircle CenterX=-120 CenterY=75 CenterZ=0 NormalX=0 NormalY=0 NormalZ=1 AngleXU=0 Radius=7 StartAngle=1.5708 EndAngle=4.71239
    g1: ArcOfCircle CenterX=-80 CenterY=75 CenterZ=0 NormalX=0 NormalY=0 NormalZ=1 AngleXU=0 Radius=7 StartAngle=4.71239 EndAngle=7.85398
    g2: LineSegment StartX=-120 StartY=68 StartZ=0 EndX=-80 EndY=68 EndZ=0
    g3: LineSegment StartX=-120 StartY=82 StartZ=0 EndX=-80 EndY=82 EndZ=0
    g4: ArcOfCircle CenterX=80 CenterY=75 CenterZ=0 NormalX=0 NormalY=0 NormalZ=1 AngleXU=0 Radius=7 StartAngle=1.5708 EndAngle=4.71239
    g5: ArcOfCircle CenterX=120 CenterY=75 CenterZ=0 NormalX=0 NormalY=0 NormalZ=1 AngleXU=0 Radius=7 StartAngle=4.71239 EndAngle=7.85398
    g6: LineSegment StartX=80 StartY=68 StartZ=0 EndX=120 EndY=68 EndZ=0
    g7: LineSegment StartX=80 StartY=82 StartZ=0 EndX=120 EndY=82 EndZ=0
    g8: LineSegment StartX=-155 StartY=110 StartZ=0 EndX=-120 EndY=75 EndZ=0
    g9: LineSegment StartX=155 StartY=110 StartZ=0 EndX=120 EndY=75 EndZ=0
  constraints (23):
    c: Tangent(g0,g3) = 1.5708
    c: Tangent(g2,g1) = -1.5708
    c: Tangent(g3,g1) = 1.5708
    c: Equal(g0,g1)
    c: Tangent(g4,g7) = 1.5708
    c: Tangent(g4,g6) = -1.5708
    c: Tangent(g6,g5) = -1.5708
    c: Tangent(g7,g5) = 1.5708
    c: Horizontal(g6)
    c: Equal(g4,g5)
    c: Symmetric(g1,g4,g-2)
    c: Equal(g1,g4)
    c: Diameter(g0) = 14
    c: Coincident(g8,g-4)
    c: Coincident(g8,g0)
    c: Coincident(g9,g-3)
    c: Coincident(g9,g5)
    c: Tangent(g0,g2) = -1.5708
    c: Horizontal(g2)
    c: DistanceX(g1,g4) = 160
    c: Equal(g6,g2)
    c: DistanceX(g2,g2) = 40
    c: DistanceY(g0,g8) = 35
FEATURE [Part::Extrusion] Extrude008
  Base = -> Sketch010
  Dir = (0,1,0)
  DirMode = 0
  FaceMakerClass = Part::FaceMakerBullseye
  LengthFwd = 50
  LengthRev = 0
  Solid = true
  Symmetric = true
FEATURE [Part::Cut] Cut003
  Base = -> Extrude006
  Refine = true
  Tool = -> Extrude008
FEATURE [Part::Extrusion] Extrude009
  Base = -> Sketch006
  Dir = (0,-2e-16,-1)
  DirMode = 2
  FaceMakerClass = Part::FaceMakerBullseye
  LengthFwd = 30
  LengthRev = 0
  Placement = pos=(0,0,39) rot=(0,0,1;0rad)
  Solid = true
  Symmetric = true
FEATURE [Part::Cut] Cut002  label="U067"
  Base = -> Extrude007
  Refine = true
  Tool = -> Extrude009
FEATURE [Part::FeaturePython] BooleanFragments002  label="BooleanFragments003"  # WARN: FeaturePython — macro-defined, semantics opaque (R4)
  Mode = 0
  Objects = -> [Extrude005,Clone004,Cut003]
  Tolerance = 0
FEATURE [Part::FeaturePython] Washer  label="M12-Washer"  # Fasteners workbench fastener (typed FeaturePython)
  Placement = pos=(120,136.482,75) rot=(-1,0,0;1.5708rad)
  diameter = 10
  invert = true
  matchOuter = false
  offset = 0
  type = 0
FEATURE [Part::FeaturePython] Screw  label="M12x120-Screw"  # Fasteners workbench fastener (typed FeaturePython)
  Placement = pos=(120,139.182,75) rot=(-1,0,0;1.5708rad)
  baseObject = -> Washer [Edge1]
  diameter = 11
  invert = false
  leftHanded = false
  length = 13
  lengthCustom = 25
  matchOuter = false
  offset = 0
  thread = false
  type = 14
FEATURE [App::DocumentObjectGroup] Group005  label="R139_219"
  Group = -> [Cut002,BooleanFragments002,BOLTS_part002,BOLTS_part003,Screw,Washer]
FEATURE [Sketcher::SketchObject] Sketch015
  FullyConstrained = true
  sketch-geometry (10):
    g0: Circle CenterX=0 CenterY=0 CenterZ=0 NormalX=0 NormalY=0 NormalZ=1 AngleXU=0 Radius=177.8
    g1: LineSegment StartX=-111.603 StartY=140.872 StartZ=0 EndX=-25 EndY=190.872 EndZ=0
    g2: LineSegment StartX=25 StartY=190.872 StartZ=0 EndX=111.603 EndY=140.872 EndZ=0
    g3: LineSegment StartX=-25 StartY=190.872 StartZ=0 EndX=25 EndY=190.872 EndZ=0
    g4: LineSegment StartX=111.603 StartY=140.872 StartZ=0 EndX=225 EndY=140.872 EndZ=0
    g5: LineSegment StartX=225 StartY=140.872 StartZ=0 EndX=225 EndY=190.872 EndZ=0
    g6: LineSegment StartX=225 StartY=190.872 StartZ=0 EndX=25 EndY=190.872 EndZ=0
    g7: LineSegment StartX=-25 StartY=190.872 StartZ=0 EndX=-225 EndY=190.872 EndZ=0
    g8: LineSegment StartX=-225 StartY=190.872 StartZ=0 EndX=-225 EndY=140.872 EndZ=0
    g9: LineSegment StartX=-225 StartY=140.872 StartZ=0 EndX=-111.603 EndY=140.872 EndZ=0
  constraints (26):
    c: Coincident(g0,g-1)
    c: Tangent(g1,g0)
    c: Symmetric(g1,g2,g-2)
    c: Symmetric(g1,g2,g-2)
    c: Coincident(g3,g1)
    c: Coincident(g3,g2)
    c: Coincident(g2,g4)
    c: Horizontal(g4)
    c: Coincident(g4,g5)
    c: Vertical(g5)
    c: Coincident(g5,g6)
    c: Coincident(g6,g2)
    c: Horizontal(g6)
    c: Coincident(g1,g7)
    c: Horizontal(g7)
    c: Coincident(g7,g8)
    c: Vertical(g8)
    c: Coincident(g8,g9)
    c: Coincident(g9,g1)
    c: Horizontal(g9)
    c: Equal(g6,g7)
    c: Angle(g-1,g1) = 0.523599
    c: Diameter(g0) = 355.6
    c: DistanceY(g5,g5) = 50
    c: DistanceX(g1,g2) = 50
    c: DistanceX(g7,g5) = 450
FEATURE [Part::Extrusion] Extrude010  label="Eckblech005"
  Base = -> Sketch015
  Dir = (0,0,1)
  DirMode = 2
  FaceMakerClass = Part::FaceMakerBullseye
  LengthFwd = 10
  LengthRev = 0
  Solid = true
  Symmetric = false
FEATURE [Part::FeaturePython] Clone005  label="Eckblech004"  # Draft clone (typed FeaturePython)
  AttacherType = Attacher::AttachEngine3D
  Fuse = false
  Objects = -> [Extrude010]
  Placement = pos=(0,0,110) rot=(0,0,1;0rad)
  Scale = (1,1,1)
FEATURE [Sketcher::SketchObject] Sketch012
  ExternalGeometry = -> [Clone005,Extrude010]
  FullyConstrained = true
  MapMode = 5
  Placement = pos=(0,190.872,0) rot=(0,0.707107,0.707107;3.14159rad)
  Support = -> [Extrude010]
  sketch-geometry (4):
    g0: LineSegment StartX=-225 StartY=0 StartZ=0 EndX=225 EndY=0 EndZ=0
    g1: LineSegment StartX=225 StartY=0 StartZ=0 EndX=225 EndY=120 EndZ=0
    g2: LineSegment StartX=225 StartY=120 StartZ=0 EndX=-225 EndY=120 EndZ=0
    g3: LineSegment StartX=-225 StartY=120 StartZ=0 EndX=-225 EndY=0 EndZ=0
  constraints (10):
    c: Coincident(g0,g1)
    c: Coincident(g1,g2)
    c: Coincident(g2,g3)
    c: Coincident(g3,g0)
    c: Horizontal(g0)
    c: Horizontal(g2)
    c: Vertical(g1)
    c: Vertical(g3)
    c: Coincident(g0,g-4)
    c: Coincident(g1,g-3)
FEATURE [Part::Extrusion] Extrude013
  Base = -> Sketch012
  Dir = (0,1,-2e-16)
  DirMode = 2
  FaceMakerClass = Part::FaceMakerBullseye
  LengthFwd = 15
  LengthRev = 0
  Solid = true
  Symmetric = false
FEATURE [Sketcher::SketchObject] Sketch013
  ExternalGeometry = -> [Extrude013]
  FullyConstrained = true
  MapMode = 5
  Placement = pos=(0,205.872,-4.94e-14) rot=(0,0.707107,0.707107;3.14159rad)
  Support = -> [Extrude013]
  sketch-geometry (13):
    g0: LineSegment StartX=-32.5 StartY=39 StartZ=0 EndX=-32.5 EndY=81 EndZ=0
    g1: LineSegment StartX=-32.5 StartY=81 StartZ=0 EndX=32.5 EndY=81 EndZ=0
    g2: LineSegment StartX=32.5 StartY=81 StartZ=0 EndX=32.5 EndY=39 EndZ=0
    g3: LineSegment StartX=-32.5 StartY=81 StartZ=0 EndX=-225 EndY=120 EndZ=0
    g4: LineSegment StartX=32.5 StartY=81 StartZ=0 EndX=225 EndY=120 EndZ=0
    g5: LineSegment StartX=-16.5 StartY=75.5 StartZ=0 EndX=16.5 EndY=75.5 EndZ=0
    g6: LineSegment StartX=23.89 StartY=69.2796 StartZ=0 EndX=28.5586 EndY=42.3175 EndZ=0
    g7: LineSegment StartX=-23.89 StartY=69.2796 StartZ=0 EndX=-28.5586 EndY=42.3175 EndZ=0
    g8: ArcOfCircle CenterX=32.5 CenterY=43 CenterZ=0 NormalX=0 NormalY=0 NormalZ=1 AngleXU=0 Radius=4 StartAngle=3.31305 EndAngle=4.71239
    g9: ArcOfCircle CenterX=16.5 CenterY=68 CenterZ=0 NormalX=0 NormalY=0 NormalZ=1 AngleXU=0 Radius=7.5 StartAngle=0.171455 EndAngle=1.5708
    g10: ArcOfCircle CenterX=-32.5 CenterY=43 CenterZ=0 NormalX=0 NormalY=0 NormalZ=1 AngleXU=0 Radius=4 StartAngle=4.71239 EndAngle=6.11173
    g11: ArcOfCircle CenterX=-16.5 CenterY=68 CenterZ=0 NormalX=0 NormalY=0 NormalZ=1 AngleXU=0 Radius=7.5 StartAngle=1.5708 EndAngle=2.97014
    g12: LineSegment StartX=-225 StartY=2.84e-14 StartZ=0 EndX=-32.5 EndY=39 EndZ=0
  constraints (35):
    c: Vertical(g0)
    c: Coincident(g0,g1)
    c: Horizontal(g1)
    c: Coincident(g1,g2)
    c: Vertical(g2)
    c: Coincident(g3,g0)
    c: Coincident(g4,g1)
    c: Coincident(g3,g-4)
    c: Coincident(g4,g-3)
    c: Equal(g3,g4)
    c: DistanceX(g1,g1) = 65
    c: DistanceY(g0,g0) = 42
    c: Equal(g0,g2)
    c: PointOnObject(g8,g2)
    c: Coincident(g8,g2)
    c: Coincident(g9,g5)
    c: Vertical(g9,g5)
    c: Tangent(g6,g9) = 1.5708
    c: Tangent(g8,g6) = -1.5708
    c: Symmetric(g5,g5,g-2)
    c: DistanceY(g5,g1) = 5.5
    c: Radius(g9) = 7.5
    c: Radius(g8) = 4
    c: DistanceX(g5,g5) = 33
    c: PointOnObject(g10,g0)
    c: Coincident(g10,g0)
    c: Coincident(g11,g5)
    c: Vertical(g11,g5)
    c: Equal(g9,g11)
    c: Tangent(g11,g7) = -1.5708
    c: Equal(g8,g10)
    c: Tangent(g10,g7) = 1.5708
    c: Coincident(g12,g-4)
    c: Coincident(g12,g0)
    c: Equal(g3,g12)
FEATURE [Sketcher::SketchObject] Sketch014
  ExternalGeometry = -> [Clone005,Extrude010]
  FullyConstrained = true
  MapMode = 5
  Placement = pos=(0,190.872,-4.58e-14) rot=(1,0,0;1.5708rad)
  Support = -> [Extrude013]
  sketch-geometry (19):
    g0: ArcOfCircle CenterX=-190 CenterY=95 CenterZ=0 NormalX=0 NormalY=0 NormalZ=1 AngleXU=0 Radius=7 StartAngle=1.5708 EndAngle=4.71239
    g1: ArcOfCircle CenterX=-135 CenterY=95 CenterZ=0 NormalX=0 NormalY=0 NormalZ=1 AngleXU=0 Radius=7 StartAngle=4.71239 EndAngle=7.85398
    g2: LineSegment StartX=-190 StartY=88 StartZ=0 EndX=-135 EndY=88 EndZ=0
    g3: LineSegment StartX=-190 StartY=102 StartZ=0 EndX=-135 EndY=102 EndZ=0
    g4: ArcOfCircle CenterX=135 CenterY=95 CenterZ=0 NormalX=0 NormalY=0 NormalZ=1 AngleXU=0 Radius=7 StartAngle=1.5708 EndAngle=4.71239
    g5: ArcOfCircle CenterX=190 CenterY=95 CenterZ=0 NormalX=0 NormalY=0 NormalZ=1 AngleXU=0 Radius=7 StartAngle=4.71239 EndAngle=7.85398
    g6: LineSegment StartX=135 StartY=88 StartZ=0 EndX=190 EndY=88 EndZ=0
    g7: LineSegment StartX=135 StartY=102 StartZ=0 EndX=190 EndY=102 EndZ=0
    g8: ArcOfCircle CenterX=-190 CenterY=25 CenterZ=0 NormalX=0 NormalY=0 NormalZ=1 AngleXU=0 Radius=7 StartAngle=1.5708 EndAngle=4.71239
    g9: ArcOfCircle CenterX=-135 CenterY=25 CenterZ=0 NormalX=0 NormalY=0 NormalZ=1 AngleXU=0 Radius=7 StartAngle=4.71239 EndAngle=7.85398
    g10: LineSegment StartX=-190 StartY=18 StartZ=0 EndX=-135 EndY=18 EndZ=0
    g11: LineSegment StartX=-190 StartY=32 StartZ=0 EndX=-135 EndY=32 EndZ=0
    g12: ArcOfCircle CenterX=135 CenterY=25 CenterZ=0 NormalX=0 NormalY=0 NormalZ=1 AngleXU=0 Radius=7 StartAngle=1.5708 EndAngle=4.71239
    g13: ArcOfCircle CenterX=190 CenterY=25 CenterZ=0 NormalX=0 NormalY=0 NormalZ=1 AngleXU=0 Radius=7 StartAngle=4.71239 EndAngle=7.85398
    g14: LineSegment StartX=135 StartY=18 StartZ=0 EndX=190 EndY=18 EndZ=0
    g15: LineSegment StartX=135 StartY=32 StartZ=0 EndX=190 EndY=32 EndZ=0
    g16: LineSegment StartX=-225 StartY=110 StartZ=0 EndX=-190 EndY=95 EndZ=0
    g17: LineSegment StartX=225 StartY=110 StartZ=0 EndX=190 EndY=95 EndZ=0
    g18: LineSegment StartX=-225 StartY=10 StartZ=0 EndX=-190 EndY=25 EndZ=0
  constraints (44):
    c: Tangent(g0,g3) = 1.5708
    c: Tangent(g2,g1) = -1.5708
    c: Tangent(g3,g1) = 1.5708
    c: Equal(g0,g1)
    c: Tangent(g4,g7) = 1.5708
    c: Tangent(g4,g6) = -1.5708
    c: Tangent(g6,g5) = -1.5708
    c: Tangent(g7,g5) = 1.5708
    c: Horizontal(g6)
    c: Equal(g4,g5)
    c: Tangent(g8,g11) = 1.5708
    c: Tangent(g8,g10) = -1.5708
    c: Tangent(g10,g9) = -1.5708
    c: Tangent(g11,g9) = 1.5708
    c: Horizontal(g10)
    c: Equal(g8,g9)
    c: Tangent(g12,g15) = 1.5708
    c: Tangent(g12,g14) = -1.5708
    c: Tangent(g14,g13) = -1.5708
    c: Tangent(g15,g13) = 1.5708
    c: Horizontal(g14)
    c: Equal(g12,g13)
    c: Symmetric(g1,g4,g-2)
    c: Symmetric(g9,g12,g-2)
    c: Vertical(g1,g9)
    c: Equal(g9,g1)
    c: Equal(g1,g4)
    c: Equal(g4,g12)
    c: Equal(g3,g11)
    c: Equal(g11,g7)
    c: Equal(g7,g15)
    c: Diameter(g0) = 14
    c: Coincident(g16,g-4)
    c: Coincident(g16,g0)
    c: Coincident(g17,g-3)
    c: Coincident(g17,g5)
    c: DistanceY(g8,g0) = 70
    c: Tangent(g0,g2) = -1.5708
    c: Horizontal(g2)
    c: Coincident(g18,g-6)
    c: Coincident(g18,g8)
    c: Equal(g16,g18)
    c: DistanceX(g11,g11) = 55
    c: DistanceX(g1,g4) = 270
FEATURE [Part::Extrusion] Extrude011
  Base = -> Sketch013
  Dir = (0,1,-2e-16)
  DirMode = 2
  FaceMakerClass = Part::FaceMakerBullseye
  LengthFwd = 135
  LengthRev = 0
  Solid = true
  Symmetric = false
FEATURE [Sketcher::SketchObject] Sketch011
  ExternalGeometry = -> [Extrude011]
  FullyConstrained = true
  MapMode = 5
  Placement = pos=(0,1.78e-14,81) rot=(0,0,1;0rad)
  Support = -> [Extrude011]
  sketch-geometry (7):
    g0: LineSegment StartX=-10 StartY=320.872 StartZ=0 EndX=10 EndY=320.872 EndZ=0
    g1: LineSegment StartX=10 StartY=320.872 StartZ=0 EndX=10 EndY=300.872 EndZ=0
    g2: LineSegment StartX=10 StartY=300.872 StartZ=0 EndX=-10 EndY=300.872 EndZ=0
    g3: LineSegment StartX=-10 StartY=300.872 StartZ=0 EndX=-10 EndY=320.872 EndZ=0
    g4: LineSegment StartX=-10 StartY=320.872 StartZ=0 EndX=-32.5 EndY=340.872 EndZ=0
    g5: LineSegment StartX=10 StartY=320.872 StartZ=0 EndX=32.5 EndY=340.872 EndZ=0
    g6: LineSegment StartX=10 StartY=310.872 StartZ=0 EndX=32.5 EndY=310.872 EndZ=0
  constraints (19):
    c: Coincident(g0,g1)
    c: Coincident(g1,g2)
    c: Coincident(g2,g3)
    c: Coincident(g3,g0)
    c: Horizontal(g0)
    c: Horizontal(g2)
    c: Vertical(g1)
    c: Vertical(g3)
    c: DistanceX(g2,g2) = 20
    c: DistanceY(g1,g1) = 20
    c: Coincident(g4,g0)
    c: Coincident(g5,g0)
    c: Coincident(g4,g-3)
    c: Coincident(g5,g-3)
    c: Equal(g4,g5)
    c: PointOnObject(g6,g1)
    c: Vertical(g5,g6)
    c: Symmetric(g1,g0,g6)
    c: DistanceY(g6,g5) = 30
FEATURE [Part::Extrusion] Extrude012
  Base = -> Sketch011
  Dir = (0,2e-16,1)
  DirMode = 2
  FaceMakerClass = Part::FaceMakerBullseye
  LengthFwd = 30
  LengthRev = 0
  Solid = true
  Symmetric = true
FEATURE [Part::Cut] Cut004  label="U068"
  Base = -> Extrude011
  Refine = true
  Tool = -> Extrude012
FEATURE [Part::Extrusion] Extrude014
  Base = -> Sketch014
  Dir = (0,1,0)
  DirMode = 0
  FaceMakerClass = Part::FaceMakerBullseye
  LengthFwd = 50
  LengthRev = 0
  Solid = true
  Symmetric = true
FEATURE [Part::Cut] Cut005
  Base = -> Extrude013
  Refine = true
  Tool = -> Extrude014
FEATURE [Part::FeaturePython] BooleanFragments003  label="BooleanFragments004"  # WARN: FeaturePython — macro-defined, semantics opaque (R4)
  Mode = 0
  Objects = -> [Extrude010,Clone005,Cut005]
  Tolerance = 0
FEATURE [Part::Cylinder] Cylinder
  Angle = 360
  AttacherType = Attacher::AttachEngine3D
  FirstAngle = 0
  Height = 250
  Placement = pos=(190,236.872,95) rot=(1,0,0;1.5708rad)
  Radius = 6
  SecondAngle = 0
FEATURE [App::DocumentObjectGroup] Group006  label="R244_355"
  Group = -> [Cut004,Cylinder,BooleanFragments003,BOLTS_part004,BOLTS_part005]
FEATURE [TechDraw::DrawSVGTemplate] Template002
  EditableTexts = AUTHOR_NAME=Axians,DN=DN,DRAWING_TITLE=Leiterhalterung,FC-DATE=06.05.2021,FC-REV=REV A,FC-SC=1:2,FC-SH=X / Y,FC-SI=A3,+6 more (map truncated)
  Height = 297
  Orientation = 1
  Width = 420
FEATURE [TechDraw::DrawProjGroupItem] ProjItem006  label="Front002"
  CoarseView = false
  Direction = (0,1,0)
  Focus = 100
  HardHidden = true
  IsoCount = 0
  IsoHidden = false
  IsoVisible = false
  LockPosition = true
  Perspective = false
  Rotation = 0
  RotationVector = (-1,0,0)
  Scale = 0.5
  ScaleType = 2
  ScrubCount = 0
  SeamHidden = false
  SeamVisible = true
  SmoothHidden = false
  SmoothVisible = true
  Source = -> [Cut004,BooleanFragments003]
  Type = 0
  X = 0
  XDirection = (-1,0,0)
  Y = 0
FEATURE [TechDraw::DrawProjGroupItem] ProjItem007  label="Left002"
  CoarseView = false
  Direction = (1,1e-16,0)
  Focus = 100
  HardHidden = true
  IsoCount = 0
  IsoHidden = false
  IsoVisible = false
  LockPosition = false
  Perspective = false
  Rotation = 0
  RotationVector = (1,0,0)
  Scale = 0.5
  ScaleType = 2
  ScrubCount = 0
  SeamHidden = false
  SeamVisible = true
  SmoothHidden = false
  SmoothVisible = true
  Source = -> [Cut004,BooleanFragments003]
  Type = 1
  X = 177.5
  XDirection = (-1e-16,1,0)
  Y = 0
FEATURE [TechDraw::DrawProjGroupItem] ProjItem008  label="Top002"
  CoarseView = false
  Direction = (0,0,1)
  Focus = 100
  HardHidden = true
  IsoCount = 0
  IsoHidden = false
  IsoVisible = false
  LockPosition = false
  Perspective = false
  Rotation = 0
  RotationVector = (1,0,0)
  Scale = 0.5
  ScaleType = 2
  ScrubCount = 0
  SeamHidden = false
  SeamVisible = true
  SmoothHidden = false
  SmoothVisible = true
  Source = -> [Cut004,BooleanFragments003]
  Type = 4
  X = 0
  XDirection = (-1,0,0)
  Y = -95
FEATURE [TechDraw::DrawProjGroup] ProjGroup002
  Anchor = -> ProjItem006
  AutoDistribute = true
  LockPosition = false
  ProjectionType = 0
  Rotation = 0
  Scale = 0.5
  ScaleType = 2
  Source = -> [Cut004,BooleanFragments003]
  Views = -> [ProjItem006,ProjItem007,ProjItem008]
  X = 147.335
  Y = 234.318
  spacingX = 15
  spacingY = 15
FEATURE [TechDraw::DrawViewBalloon] Balloon002
  BubbleShape = 0
  EndType = 0
  EndTypeScale = 1
  KinkLength = 5
  LockPosition = false
  OriginX = 21.878
  OriginY = -87.9268
  Rotation = 0
  Scale = 0.2
  ScaleType = 2
  ShapeScale = 1
  SourceView = -> ProjItem008
  Text = 1
  TextWrapLen = -1
  X = 61.878
  Y = -47.9268
FEATURE [TechDraw::DrawViewAnnotation] Annotation002
  Font = Arial
  LineSpace = 80
  LockPosition = false
  MaxWidth = -1
  Rotation = 0
  Scale = 0.2
  ScaleType = 2
  Text = U-65
  TextSize = 5
  TextStyle = 0
  X = 186.77
  Y = 97.0772
FEATURE [TechDraw::DrawViewDimension] Dimension024
  AngleOverride = false
  Arbitrary = false
  ArbitraryTolerances = false
  EqualTolerance = true
  ExtensionAngle = 0
  FormatSpec = %.1f
  FormatSpecOverTolerance = %+.1f
  FormatSpecUnderTolerance = %+.1f
  Inverted = false
  LineAngle = 0
  LockPosition = false
  MeasureType = 1
  OverTolerance = 0
  References2D = -> [ProjItem006]
  Rotation = 0
  Scale = 0.2
  ScaleType = 2
  TheoreticalExact = false
  Type = 1
  UnderTolerance = 0
  X = 0.402439
  Y = 39.6585
FEATURE [TechDraw::DrawViewDimension] Dimension025
  AngleOverride = false
  Arbitrary = false
  ArbitraryTolerances = false
  EqualTolerance = true
  ExtensionAngle = 0
  FormatSpec = %.1f
  FormatSpecOverTolerance = %+.1f
  FormatSpecUnderTolerance = %+.1f
  Inverted = false
  LineAngle = 0
  LockPosition = false
  MeasureType = 1
  OverTolerance = 0
  References2D = -> [ProjItem006]
  Rotation = 0
  Scale = 0.2
  ScaleType = 2
  TheoreticalExact = false
  Type = 2
  UnderTolerance = 0
  X = -120.146
  Y = -1.20732
FEATURE [TechDraw::DrawViewDimension] Dimension026
  AngleOverride = false
  Arbitrary = false
  ArbitraryTolerances = false
  EqualTolerance = true
  ExtensionAngle = 0
  FormatSpec = %.1f
  FormatSpecOverTolerance = %+.1f
  FormatSpecUnderTolerance = %+.1f
  Inverted = false
  LineAngle = 0
  LockPosition = false
  MeasureType = 1
  OverTolerance = 0
  References2D = -> [ProjItem008]
  Rotation = 0
  Scale = 0.2
  ScaleType = 2
  TheoreticalExact = false
  Type = 6
  UnderTolerance = 0
  X = 88.7841
  Y = 60.3659
FEATURE [TechDraw::DrawViewDimension] Dimension027
  AngleOverride = false
  Arbitrary = false
  ArbitraryTolerances = false
  EqualTolerance = true
  ExtensionAngle = 0
  FormatSpec = %.1f
  FormatSpecOverTolerance = %+.1f
  FormatSpecUnderTolerance = %+.1f
  Inverted = false
  LineAngle = 0
  LockPosition = false
  MeasureType = 1
  OverTolerance = 0
  References2D = -> [ProjItem008]
  Rotation = 0
  Scale = 0.2
  ScaleType = 2
  TheoreticalExact = false
  Type = 2
  UnderTolerance = 0
  X = 130.207
  Y = 37.5
FEATURE [TechDraw::DrawViewDimension] Dimension028
  AngleOverride = false
  Arbitrary = false
  ArbitraryTolerances = false
  EqualTolerance = true
  ExtensionAngle = 0
  FormatSpec = %.1f
  FormatSpecOverTolerance = %+.1f
  FormatSpecUnderTolerance = %+.1f
  Inverted = false
  LineAngle = 0
  LockPosition = false
  MeasureType = 1
  OverTolerance = 0
  References2D = -> [ProjItem008]
  Rotation = 0
  Scale = 0.2
  ScaleType = 2
  TheoreticalExact = false
  Type = 2
  UnderTolerance = 0
  X = 121.354
  Y = 5.55488
FEATURE [TechDraw::DrawViewDimension] Dimension029
  AngleOverride = false
  Arbitrary = false
  ArbitraryTolerances = false
  EqualTolerance = true
  ExtensionAngle = 0
  FormatSpec = %.1f
  FormatSpecOverTolerance = %+.1f
  FormatSpecUnderTolerance = %+.1f
  Inverted = false
  LineAngle = 0
  LockPosition = false
  MeasureType = 1
  OverTolerance = 0
  References2D = -> [ProjItem007]
  Rotation = 0
  Scale = 0.2
  ScaleType = 2
  TheoreticalExact = false
  Type = 2
  UnderTolerance = 0
  X = -42.431
  Y = 40.6973
FEATURE [TechDraw::DrawViewDimension] Dimension030
  AngleOverride = false
  Arbitrary = false
  ArbitraryTolerances = false
  EqualTolerance = true
  ExtensionAngle = 0
  FormatSpec = %.1f
  FormatSpecOverTolerance = %+.1f
  FormatSpecUnderTolerance = %+.1f
  Inverted = false
  LineAngle = 0
  LockPosition = false
  MeasureType = 1
  OverTolerance = 0
  References2D = -> [ProjItem007]
  Rotation = 0
  Scale = 0.2
  ScaleType = 2
  TheoreticalExact = false
  Type = 1
  UnderTolerance = 0
  X = 13.311
  Y = 46.1354
FEATURE [TechDraw::DrawViewDimension] Dimension031
  AngleOverride = false
  Arbitrary = false
  ArbitraryTolerances = false
  EqualTolerance = true
  ExtensionAngle = 0
  FormatSpec = %.1f
  FormatSpecOverTolerance = %+.1f
  FormatSpecUnderTolerance = %+.1f
  Inverted = false
  LineAngle = 0
  LockPosition = false
  MeasureType = 1
  OverTolerance = 0
  References2D = -> [ProjItem008]
  Rotation = 0
  Scale = 0.2
  ScaleType = 2
  TheoreticalExact = false
  Type = 1
  UnderTolerance = 0
  X = 0.367375
  Y = 65.0439
FEATURE [TechDraw::DrawViewDimension] Dimension032
  AngleOverride = false
  Arbitrary = false
  ArbitraryTolerances = false
  EqualTolerance = true
  ExtensionAngle = 0
  FormatSpec = %.1f
  FormatSpecOverTolerance = %+.1f
  FormatSpecUnderTolerance = %+.1f
  Inverted = false
  LineAngle = 0
  LockPosition = false
  MeasureType = 1
  OverTolerance = 0
  References2D = -> [ProjItem008]
  Rotation = 0
  Scale = 0.2
  ScaleType = 2
  TheoreticalExact = false
  Type = 1
  UnderTolerance = 0
  X = -60.8232
  Y = 64.4055
FEATURE [TechDraw::DrawPage] Page002  label="Page_R244_355"
  KeepUpdated = true
  NextBalloonIndex = 2
  ProjectionType = 0
  Template = -> Template002
  Views = -> [ProjGroup002,Balloon002,Annotation002,Dimension024,Dimension025,Dimension026,Dimension027,Dimension028,Dimension029,Dimension030,Dimension031,Dimension032]
FEATURE [Part::Cylinder] Cylinder001
  Angle = 360
  AttacherType = Attacher::AttachEngine3D
  FirstAngle = 0
  Height = 500
  Placement = pos=(325,376.863,95) rot=(1,0,0;1.5708rad)
  Radius = 6
  SecondAngle = 0
FEATURE [Sketcher::SketchObject] Sketch020
  FullyConstrained = true
  sketch-geometry (10):
    g0: Circle CenterX=0 CenterY=0 CenterZ=0 NormalX=0 NormalY=0 NormalZ=1 AngleXU=0 Radius=305
    g1: LineSegment StartX=-185.885 StartY=244.863 StartZ=0 EndX=-30 EndY=334.863 EndZ=0
    g2: LineSegment StartX=30 StartY=334.863 StartZ=0 EndX=185.885 EndY=244.863 EndZ=0
    g3: LineSegment StartX=-30 StartY=334.863 StartZ=0 EndX=30 EndY=334.863 EndZ=0
    g4: LineSegment StartX=185.885 StartY=244.863 StartZ=0 EndX=385 EndY=244.863 EndZ=0
    g5: LineSegment StartX=385 StartY=244.863 StartZ=0 EndX=385 EndY=334.863 EndZ=0
    g6: LineSegment StartX=385 StartY=334.863 StartZ=0 EndX=30 EndY=334.863 EndZ=0
    g7: LineSegment StartX=-30 StartY=334.863 StartZ=0 EndX=-385 EndY=334.863 EndZ=0
    g8: LineSegment StartX=-385 StartY=334.863 StartZ=0 EndX=-385 EndY=244.863 EndZ=0
    g9: LineSegment StartX=-385 StartY=244.863 StartZ=0 EndX=-185.885 EndY=244.863 EndZ=0
  constraints (26):
    c: Coincident(g0,g-1)
    c: Tangent(g1,g0)
    c: Symmetric(g1,g2,g-2)
    c: Symmetric(g1,g2,g-2)
    c: Coincident(g3,g1)
    c: Coincident(g3,g2)
    c: Coincident(g2,g4)
    c: Horizontal(g4)
    c: Coincident(g4,g5)
    c: Vertical(g5)
    c: Coincident(g5,g6)
    c: Coincident(g6,g2)
    c: Horizontal(g6)
    c: Coincident(g1,g7)
    c: Horizontal(g7)
    c: Coincident(g7,g8)
    c: Vertical(g8)
    c: Coincident(g8,g9)
    c: Coincident(g9,g1)
    c: Horizontal(g9)
    c: Equal(g6,g7)
    c: Angle(g-1,g1) = 0.523599
    c: Diameter(g0) = 610
    c: DistanceX(g3,g3) = 60
    c: DistanceY(g5,g5) = 90
    c: DistanceX(g7,g5) = 770
FEATURE [Part::Extrusion] Extrude019  label="Eckblech006"
  Base = -> Sketch020
  Dir = (0,0,1)
  DirMode = 2
  FaceMakerClass = Part::FaceMakerBullseye
  LengthFwd = 10
  LengthRev = 0
  Solid = true
  Symmetric = false
FEATURE [Part::FeaturePython] Clone006  label="Eckblech007"  # Draft clone (typed FeaturePython)
  AttacherType = Attacher::AttachEngine3D
  Fuse = false
  Objects = -> [Extrude019]
  Placement = pos=(0,0,110) rot=(0,0,1;0rad)
  Scale = (1,1,1)
FEATURE [Sketcher::SketchObject] Sketch016
  ExternalGeometry = -> [Clone006,Extrude019]
  FullyConstrained = true
  MapMode = 5
  Placement = pos=(0,334.863,0) rot=(0,0.707107,0.707107;3.14159rad)
  Support = -> [Extrude019]
  sketch-geometry (4):
    g0: LineSegment StartX=-385 StartY=0 StartZ=0 EndX=385 EndY=0 EndZ=0
    g1: LineSegment StartX=385 StartY=0 StartZ=0 EndX=385 EndY=120 EndZ=0
    g2: LineSegment StartX=385 StartY=120 StartZ=0 EndX=-385 EndY=120 EndZ=0
    g3: LineSegment StartX=-385 StartY=120 StartZ=0 EndX=-385 EndY=0 EndZ=0
  constraints (10):
    c: Coincident(g0,g1)
    c: Coincident(g1,g2)
    c: Coincident(g2,g3)
    c: Coincident(g3,g0)
    c: Horizontal(g0)
    c: Horizontal(g2)
    c: Vertical(g1)
    c: Vertical(g3)
    c: Coincident(g0,g-4)
    c: Coincident(g1,g-3)
FEATURE [Part::Extrusion] Extrude015
  Base = -> Sketch016
  Dir = (0,1,-2e-16)
  DirMode = 2
  FaceMakerClass = Part::FaceMakerBullseye
  LengthFwd = 15
  LengthRev = 0
  Solid = true
  Symmetric = false
FEATURE [Sketcher::SketchObject] Sketch018
  ExternalGeometry = -> [Clone006,Extrude019]
  FullyConstrained = true
  MapMode = 5
  Placement = pos=(0,334.863,0) rot=(1,0,0;1.5708rad)
  Support = -> [Extrude015]
  sketch-geometry (36):
    g0: ArcOfCircle CenterX=-265 CenterY=95 CenterZ=0 NormalX=0 NormalY=0 NormalZ=1 AngleXU=0 Radius=7 StartAngle=1.5708 EndAngle=4.71239
    g1: ArcOfCircle CenterX=-215 CenterY=95 CenterZ=0 NormalX=0 NormalY=0 NormalZ=1 AngleXU=0 Radius=7 StartAngle=4.71239 EndAngle=7.85398
    g2: LineSegment StartX=-265 StartY=88 StartZ=0 EndX=-215 EndY=88 EndZ=0
    g3: LineSegment StartX=-265 StartY=102 StartZ=0 EndX=-215 EndY=102 EndZ=0
    g4: ArcOfCircle CenterX=215 CenterY=95 CenterZ=0 NormalX=0 NormalY=0 NormalZ=1 AngleXU=0 Radius=7 StartAngle=1.5708 EndAngle=4.71239
    g5: ArcOfCircle CenterX=265 CenterY=95 CenterZ=0 NormalX=0 NormalY=0 NormalZ=1 AngleXU=0 Radius=7 StartAngle=4.71239 EndAngle=7.85398
    g6: LineSegment StartX=215 StartY=88 StartZ=0 EndX=265 EndY=88 EndZ=0
    g7: LineSegment StartX=215 StartY=102 StartZ=0 EndX=265 EndY=102 EndZ=0
    g8: ArcOfCircle CenterX=-265 CenterY=25 CenterZ=0 NormalX=0 NormalY=0 NormalZ=1 AngleXU=0 Radius=7 StartAngle=1.5708 EndAngle=4.71239
    g9: ArcOfCircle CenterX=-215 CenterY=25 CenterZ=0 NormalX=0 NormalY=0 NormalZ=1 AngleXU=0 Radius=7 StartAngle=4.71239 EndAngle=7.85398
    g10: LineSegment StartX=-265 StartY=18 StartZ=0 EndX=-215 EndY=18 EndZ=0
    g11: LineSegment StartX=-265 StartY=32 StartZ=0 EndX=-215 EndY=32 EndZ=0
    g12: ArcOfCircle CenterX=215 CenterY=25 CenterZ=0 NormalX=0 NormalY=0 NormalZ=1 AngleXU=0 Radius=7 StartAngle=1.5708 EndAngle=4.71239
    g13: ArcOfCircle CenterX=265 CenterY=25 CenterZ=0 NormalX=0 NormalY=0 NormalZ=1 AngleXU=0 Radius=7 StartAngle=4.71239 EndAngle=7.85398
    g14: LineSegment StartX=215 StartY=18 StartZ=0 EndX=265 EndY=18 EndZ=0
    g15: LineSegment StartX=215 StartY=32 StartZ=0 EndX=265 EndY=32 EndZ=0
    g16: LineSegment StartX=-385 StartY=110 StartZ=0 EndX=-265 EndY=95 EndZ=0
    g17: LineSegment StartX=385 StartY=110 StartZ=0 EndX=265 EndY=95 EndZ=0
    g18: LineSegment StartX=-385 StartY=10 StartZ=0 EndX=-265 EndY=25 EndZ=0
    g19: ArcOfCircle CenterX=-265 CenterY=95 CenterZ=0 NormalX=0 NormalY=0 NormalZ=1 AngleXU=0 Radius=7 StartAngle=2e-16 EndAngle=1.5708
    g20: ArcOfCircle CenterX=-325 CenterY=95 CenterZ=0 NormalX=0 NormalY=0 NormalZ=1 AngleXU=0 Radius=7 StartAngle=1.5708 EndAngle=4.71239
    g21: ArcOfCircle CenterX=-310 CenterY=95 CenterZ=0 NormalX=0 NormalY=0 NormalZ=1 AngleXU=0 Radius=7 StartAngle=4.71239 EndAngle=7.85398
    g22: LineSegment StartX=-325 StartY=88 StartZ=0 EndX=-310 EndY=88 EndZ=0
    g23: LineSegment StartX=-325 StartY=102 StartZ=0 EndX=-310 EndY=102 EndZ=0
    g24: ArcOfCircle CenterX=-325 CenterY=25 CenterZ=0 NormalX=0 NormalY=0 NormalZ=1 AngleXU=0 Radius=7 StartAngle=1.5708 EndAngle=4.71239
    g25: ArcOfCircle CenterX=-310 CenterY=25 CenterZ=0 NormalX=0 NormalY=0 NormalZ=1 AngleXU=0 Radius=7 StartAngle=4.71239 EndAngle=7.85398
    g26: LineSegment StartX=-325 StartY=18 StartZ=0 EndX=-310 EndY=18 EndZ=0
    g27: LineSegment StartX=-325 StartY=32 StartZ=0 EndX=-310 EndY=32 EndZ=0
    g28: ArcOfCircle CenterX=310 CenterY=95 CenterZ=0 NormalX=0 NormalY=0 NormalZ=1 AngleXU=0 Radius=7 StartAngle=1.5708 EndAngle=4.71239
    g29: ArcOfCircle CenterX=325 CenterY=95 CenterZ=0 NormalX=0 NormalY=0 NormalZ=1 AngleXU=0 Radius=7 StartAngle=4.71239 EndAngle=7.85398
    g30: LineSegment StartX=310 StartY=88 StartZ=0 EndX=325 EndY=88 EndZ=0
    g31: LineSegment StartX=310 StartY=102 StartZ=0 EndX=325 EndY=102 EndZ=0
    g32: ArcOfCircle CenterX=310 CenterY=25 CenterZ=0 NormalX=0 NormalY=0 NormalZ=1 AngleXU=0 Radius=7 StartAngle=1.5708 EndAngle=4.71239
    g33: ArcOfCircle CenterX=325 CenterY=25 CenterZ=0 NormalX=0 NormalY=0 NormalZ=1 AngleXU=0 Radius=7 StartAngle=4.71239 EndAngle=7.85398
    g34: LineSegment StartX=310 StartY=18 StartZ=0 EndX=325 EndY=18 EndZ=0
    g35: LineSegment StartX=310 StartY=32 StartZ=0 EndX=325 EndY=32 EndZ=0
  constraints (85):
    c: Tangent(g0,g3) = 1.5708
    c: Tangent(g2,g1) = -1.5708
    c: Tangent(g3,g1) = 1.5708
    c: Equal(g0,g1)
    c: Tangent(g4,g7) = 1.5708
    c: Tangent(g4,g6) = -1.5708
    c: Tangent(g6,g5) = -1.5708
    c: Tangent(g7,g5) = 1.5708
    c: Horizontal(g6)
    c: Equal(g4,g5)
    c: Tangent(g8,g11) = 1.5708
    c: Tangent(g8,g10) = -1.5708
    c: Tangent(g10,g9) = -1.5708
    c: Tangent(g11,g9) = 1.5708
    c: Horizontal(g10)
    c: Equal(g8,g9)
    c: Tangent(g12,g15) = 1.5708
    c: Tangent(g12,g14) = -1.5708
    c: Tangent(g14,g13) = -1.5708
    c: Tangent(g15,g13) = 1.5708
    c: Horizontal(g14)
    c: Equal(g12,g13)
    c: Symmetric(g1,g4,g-2)
    c: Symmetric(g9,g12,g-2)
    c: Vertical(g1,g9)
    c: Equal(g9,g1)
    c: Equal(g1,g4)
    c: Equal(g4,g12)
    c: Equal(g3,g11)
    c: Equal(g11,g7)
    c: Equal(g7,g15)
    c: Diameter(g0) = 14
    c: Coincident(g16,g-4)
    c: Coincident(g16,g0)
    c: Coincident(g17,g-3)
    c: Coincident(g17,g5)
    c: DistanceY(g8,g0) = 70
    c: Tangent(g0,g2) = -1.5708
    c: Horizontal(g2)
    c: Coincident(g18,g-6)
    c: Coincident(g18,g8)
    c: Equal(g16,g18)
    c: Coincident(g19,g0)
    c: Coincident(g19,g0)
    c: Horizontal(g19,g0)
    c: DistanceX(g3,g3) = 50
    c: DistanceX(g1,g4) = 430
    c: Tangent(g20,g23) = 1.5708
    c: Tangent(g20,g22) = -1.5708
    c: Tangent(g22,g21) = -1.5708
    c: Tangent(g23,g21) = 1.5708
    c: Horizontal(g22)
    c: Equal(g20,g21)
    c: Tangent(g24,g27) = 1.5708
    c: Tangent(g24,g26) = -1.5708
    c: Tangent(g26,g25) = -1.5708
    c: Tangent(g27,g25) = 1.5708
    c: Horizontal(g26)
    c: Equal(g24,g25)
    c: Tangent(g28,g31) = 1.5708
    c: Tangent(g28,g30) = -1.5708
    c: Tangent(g30,g29) = -1.5708
    c: Tangent(g31,g29) = 1.5708
    c: Horizontal(g30)
    c: Equal(g28,g29)
    c: Tangent(g32,g35) = 1.5708
    c: Tangent(g32,g34) = -1.5708
    c: Tangent(g34,g33) = -1.5708
    c: Tangent(g35,g33) = 1.5708
    c: Horizontal(g34)
    c: Equal(g32,g33)
    c: Equal(g22,g27)
    c: Equal(g27,g30)
    c: Equal(g30,g35)
    c: Equal(g0,g21)
    c: Equal(g21,g25)
    c: Equal(g25,g28)
    c: Equal(g28,g32)
    c: Symmetric(g28,g21,g-2)
    c: Horizontal(g21,g0)
    c: Symmetric(g32,g25,g-2)
    c: Vertical(g21,g25)
    c: DistanceX(g22,g22) = 15
    c: Horizontal(g25,g8)
    c: DistanceX(g13,g32) = 45
FEATURE [Part::Extrusion] Extrude018
  Base = -> Sketch018
  Dir = (0,1,0)
  DirMode = 0
  FaceMakerClass = Part::FaceMakerBullseye
  LengthFwd = 50
  LengthRev = 0
  Solid = true
  Symmetric = true
FEATURE [Part::Cut] Cut007
  Base = -> Extrude015
  Refine = true
  Tool = -> Extrude018
FEATURE [Part::FeaturePython] BooleanFragments004  label="BooleanFragments005"  # WARN: FeaturePython — macro-defined, semantics opaque (R4)
  Mode = 0
  Objects = -> [Extrude019,Clone006,Cut007]
  Tolerance = 0
FEATURE [Sketcher::SketchObject] Sketch019
  ExternalGeometry = -> [Extrude015]
  FullyConstrained = true
  MapMode = 5
  Placement = pos=(0,349.863,0) rot=(0,0.707107,0.707107;3.14159rad)
  Support = -> [Extrude015]
  sketch-geometry (13):
    g0: LineSegment StartX=-32.5 StartY=39 StartZ=0 EndX=-32.5 EndY=81 EndZ=0
    g1: LineSegment StartX=-32.5 StartY=81 StartZ=0 EndX=32.5 EndY=81 EndZ=0
    g2: LineSegment StartX=32.5 StartY=81 StartZ=0 EndX=32.5 EndY=39 EndZ=0
    g3: LineSegment StartX=-32.5 StartY=81 StartZ=0 EndX=-385 EndY=120 EndZ=0
    g4: LineSegment StartX=32.5 StartY=81 StartZ=0 EndX=385 EndY=120 EndZ=0
    g5: LineSegment StartX=-16.5 StartY=75.5 StartZ=0 EndX=16.5 EndY=75.5 EndZ=0
    g6: LineSegment StartX=23.89 StartY=69.2796 StartZ=0 EndX=28.5586 EndY=42.3175 EndZ=0
    g7: LineSegment StartX=-23.89 StartY=69.2796 StartZ=0 EndX=-28.5586 EndY=42.3175 EndZ=0
    g8: ArcOfCircle CenterX=32.5 CenterY=43 CenterZ=0 NormalX=0 NormalY=0 NormalZ=1 AngleXU=0 Radius=4 StartAngle=3.31305 EndAngle=4.71239
    g9: ArcOfCircle CenterX=16.5 CenterY=68 CenterZ=0 NormalX=0 NormalY=0 NormalZ=1 AngleXU=0 Radius=7.5 StartAngle=0.171455 EndAngle=1.5708
    g10: ArcOfCircle CenterX=-32.5 CenterY=43 CenterZ=0 NormalX=0 NormalY=0 NormalZ=1 AngleXU=0 Radius=4 StartAngle=4.71239 EndAngle=6.11173
    g11: ArcOfCircle CenterX=-16.5 CenterY=68 CenterZ=0 NormalX=0 NormalY=0 NormalZ=1 AngleXU=0 Radius=7.5 StartAngle=1.5708 EndAngle=2.97014
    g12: LineSegment StartX=-385 StartY=0 StartZ=0 EndX=-32.5 EndY=39 EndZ=0
  constraints (35):
    c: Vertical(g0)
    c: Coincident(g0,g1)
    c: Horizontal(g1)
    c: Coincident(g1,g2)
    c: Vertical(g2)
    c: Coincident(g3,g0)
    c: Coincident(g4,g1)
    c: Coincident(g3,g-4)
    c: Coincident(g4,g-3)
    c: Equal(g3,g4)
    c: DistanceX(g1,g1) = 65
    c: DistanceY(g0,g0) = 42
    c: Equal(g0,g2)
    c: PointOnObject(g8,g2)
    c: Coincident(g8,g2)
    c: Coincident(g9,g5)
    c: Vertical(g9,g5)
    c: Tangent(g6,g9) = 1.5708
    c: Tangent(g8,g6) = -1.5708
    c: Symmetric(g5,g5,g-2)
    c: DistanceY(g5,g1) = 5.5
    c: Radius(g9) = 7.5
    c: Radius(g8) = 4
    c: DistanceX(g5,g5) = 33
    c: PointOnObject(g10,g0)
    c: Coincident(g10,g0)
    c: Coincident(g11,g5)
    c: Vertical(g11,g5)
    c: Equal(g9,g11)
    c: Tangent(g11,g7) = -1.5708
    c: Equal(g8,g10)
    c: Tangent(g10,g7) = 1.5708
    c: Coincident(g12,g-4)
    c: Coincident(g12,g0)
    c: Equal(g3,g12)
FEATURE [Part::Extrusion] Extrude017
  Base = -> Sketch019
  Dir = (0,1,-2e-16)
  DirMode = 2
  FaceMakerClass = Part::FaceMakerBullseye
  LengthFwd = 135
  LengthRev = 0
  Solid = true
  Symmetric = false
FEATURE [Sketcher::SketchObject] Sketch017
  ExternalGeometry = -> [Extrude017]
  FullyConstrained = true
  MapMode = 5
  Placement = pos=(0,1.78e-14,81) rot=(0,0,1;0rad)
  Support = -> [Extrude017]
  sketch-geometry (7):
    g0: LineSegment StartX=-10 StartY=464.863 StartZ=0 EndX=10 EndY=464.863 EndZ=0
    g1: LineSegment StartX=10 StartY=464.863 StartZ=0 EndX=10 EndY=444.863 EndZ=0
    g2: LineSegment StartX=10 StartY=444.863 StartZ=0 EndX=-10 EndY=444.863 EndZ=0
    g3: LineSegment StartX=-10 StartY=444.863 StartZ=0 EndX=-10 EndY=464.863 EndZ=0
    g4: LineSegment StartX=-10 StartY=464.863 StartZ=0 EndX=-32.5 EndY=484.863 EndZ=0
    g5: LineSegment StartX=10 StartY=464.863 StartZ=0 EndX=32.5 EndY=484.863 EndZ=0
    g6: LineSegment StartX=10 StartY=454.863 StartZ=0 EndX=32.5 EndY=454.863 EndZ=0
  constraints (19):
    c: Coincident(g0,g1)
    c: Coincident(g1,g2)
    c: Coincident(g2,g3)
    c: Coincident(g3,g0)
    c: Horizontal(g0)
    c: Horizontal(g2)
    c: Vertical(g1)
    c: Vertical(g3)
    c: DistanceX(g2,g2) = 20
    c: DistanceY(g1,g1) = 20
    c: Coincident(g4,g0)
    c: Coincident(g5,g0)
    c: Coincident(g4,g-3)
    c: Coincident(g5,g-3)
    c: Equal(g4,g5)
    c: PointOnObject(g6,g1)
    c: Vertical(g5,g6)
    c: Symmetric(g1,g0,g6)
    c: DistanceY(g6,g5) = 30
FEATURE [Part::Extrusion] Extrude016
  Base = -> Sketch017
  Dir = (0,2e-16,1)
  DirMode = 2
  FaceMakerClass = Part::FaceMakerBullseye
  LengthFwd = 30
  LengthRev = 0
  Solid = true
  Symmetric = true
FEATURE [Part::Cut] Cut006  label="U069"
  Base = -> Extrude017
  Refine = true
  Tool = -> Extrude016
FEATURE [Part::Feature] BOLTS_part009  label="Circular hollow profile 508.0/10.0 l=360.0"
  Placement = pos=(0,0,-120) rot=(0,0,1;0rad)
  shape: bbox 508 x 508 x 360 mm, 4 faces (baked)
FEATURE [App::DocumentObjectGroup] Group007  label="R406_508_610"
  Group = -> [Cylinder001,Cut006,BooleanFragments004,BOLTS_part006,BOLTS_part007,BOLTS_part009]
FEATURE [TechDraw::DrawSVGTemplate] Template003
  EditableTexts = AUTHOR_NAME=Axians,DN=DN,DRAWING_TITLE=Leiterhalterung,FC-DATE=07.05.2021,FC-REV=REV A,FC-SC=1:5,FC-SH=X / Y,FC-SI=A3,+6 more (map truncated)
  Height = 297
  Orientation = 1
  Width = 420
FEATURE [TechDraw::DrawProjGroupItem] ProjItem009  label="Front003"
  CoarseView = false
  Direction = (0,1,0)
  Focus = 100
  HardHidden = true
  IsoCount = 0
  IsoHidden = false
  IsoVisible = false
  LockPosition = true
  Perspective = false
  Rotation = 0
  RotationVector = (-1,0,0)
  Scale = 0.2
  ScaleType = 2
  ScrubCount = 0
  SeamHidden = false
  SeamVisible = true
  SmoothHidden = false
  SmoothVisible = true
  Source = -> [Cut006,BooleanFragments004]
  Type = 0
  X = 0
  XDirection = (-1,0,0)
  Y = 0
FEATURE [TechDraw::DrawProjGroupItem] ProjItem010  label="Left003"
  CoarseView = false
  Direction = (1,1e-16,0)
  Focus = 100
  HardHidden = true
  IsoCount = 0
  IsoHidden = false
  IsoVisible = false
  LockPosition = false
  Perspective = false
  Rotation = 0
  RotationVector = (1,0,0)
  Scale = 0.2
  ScaleType = 2
  ScrubCount = 0
  SeamHidden = false
  SeamVisible = true
  SmoothHidden = false
  SmoothVisible = true
  Source = -> [Cut006,BooleanFragments004]
  Type = 1
  X = 116
  XDirection = (-1e-16,1,0)
  Y = 0
FEATURE [TechDraw::DrawProjGroupItem] ProjItem011  label="Top003"
  CoarseView = false
  Direction = (0,0,1)
  Focus = 100
  HardHidden = true
  IsoCount = 0
  IsoHidden = false
  IsoVisible = false
  LockPosition = false
  Perspective = false
  Rotation = 0
  RotationVector = (1,0,0)
  Scale = 0.2
  ScaleType = 2
  ScrubCount = 0
  SeamHidden = false
  SeamVisible = true
  SmoothHidden = false
  SmoothVisible = true
  Source = -> [Cut006,BooleanFragments004]
  Type = 4
  X = 0
  XDirection = (-1,0,0)
  Y = -51
FEATURE [TechDraw::DrawProjGroup] ProjGroup003
  Anchor = -> ProjItem009
  AutoDistribute = true
  LockPosition = false
  ProjectionType = 0
  Rotation = 0
  Scale = 0.2
  ScaleType = 2
  Source = -> [Cut006,BooleanFragments004]
  Views = -> [ProjItem009,ProjItem010,ProjItem011]
  X = 138.768
  Y = 203.634
  spacingX = 15
  spacingY = 15
FEATURE [TechDraw::DrawViewDimension] Dimension033
  AngleOverride = false
  Arbitrary = false
  ArbitraryTolerances = false
  EqualTolerance = true
  ExtensionAngle = 0
  FormatSpec = %.1f
  FormatSpecOverTolerance = %+.1f
  FormatSpecUnderTolerance = %+.1f
  Inverted = false
  LineAngle = 0
  LockPosition = false
  MeasureType = 1
  OverTolerance = 0
  References2D = -> [ProjItem009]
  Rotation = 0
  Scale = 0.2
  ScaleType = 2
  TheoreticalExact = false
  Type = 1
  UnderTolerance = 0
  X = -0.377373
  Y = 32.0601
FEATURE [TechDraw::DrawViewDimension] Dimension034
  AngleOverride = false
  Arbitrary = false
  ArbitraryTolerances = false
  EqualTolerance = true
  ExtensionAngle = 0
  FormatSpec = %.1f
  FormatSpecOverTolerance = %+.1f
  FormatSpecUnderTolerance = %+.1f
  Inverted = false
  LineAngle = 0
  LockPosition = false
  MeasureType = 1
  OverTolerance = 0
  References2D = -> [ProjItem009]
  Rotation = 0
  Scale = 0.2
  ScaleType = 2
  TheoreticalExact = false
  Type = 2
  UnderTolerance = 0
  X = -90.3913
  Y = 0.388155
FEATURE [TechDraw::DrawViewDimension] Dimension035
  AngleOverride = false
  Arbitrary = false
  ArbitraryTolerances = false
  EqualTolerance = true
  ExtensionAngle = 0
  FormatSpec = %.1f
  FormatSpecOverTolerance = %+.1f
  FormatSpecUnderTolerance = %+.1f
  Inverted = false
  LineAngle = 0
  LockPosition = false
  MeasureType = 1
  OverTolerance = 0
  References2D = -> [ProjItem010]
  Rotation = 0
  Scale = 0.2
  ScaleType = 2
  TheoreticalExact = false
  Type = 2
  UnderTolerance = 0
  X = -31.8249
  Y = 23.5494
FEATURE [TechDraw::DrawViewDimension] Dimension036
  AngleOverride = false
  Arbitrary = false
  ArbitraryTolerances = false
  EqualTolerance = true
  ExtensionAngle = 0
  FormatSpec = %.1f
  FormatSpecOverTolerance = %+.1f
  FormatSpecUnderTolerance = %+.1f
  Inverted = false
  LineAngle = 0
  LockPosition = false
  MeasureType = 1
  OverTolerance = 0
  References2D = -> [ProjItem010]
  Rotation = 0
  Scale = 0.2
  ScaleType = 2
  TheoreticalExact = false
  Type = 1
  UnderTolerance = 0
  X = -18.3781
  Y = 22.1871
FEATURE [TechDraw::DrawViewDimension] Dimension037
  AngleOverride = false
  Arbitrary = false
  ArbitraryTolerances = false
  EqualTolerance = true
  ExtensionAngle = 0
  FormatSpec = %.1f
  FormatSpecOverTolerance = %+.1f
  FormatSpecUnderTolerance = %+.1f
  Inverted = false
  LineAngle = 0
  LockPosition = false
  MeasureType = 1
  OverTolerance = 0
  References2D = -> [ProjItem009]
  Rotation = 0
  Scale = 0.2
  ScaleType = 2
  TheoreticalExact = false
  Type = 2
  UnderTolerance = 0
  X = -74.2275
  Y = 0.854397
FEATURE [TechDraw::DrawViewDimension] Dimension038
  AngleOverride = false
  Arbitrary = false
  ArbitraryTolerances = false
  EqualTolerance = true
  ExtensionAngle = 0
  FormatSpec = ⌀%.1f
  FormatSpecOverTolerance = %+.1f
  FormatSpecUnderTolerance = %+.1f
  Inverted = false
  LineAngle = 0
  LockPosition = false
  MeasureType = 1
  OverTolerance = 0
  References2D = -> [ProjItem009]
  Rotation = 0
  Scale = 0.2
  ScaleType = 2
  TheoreticalExact = false
  Type = 5
  UnderTolerance = 0
  X = 82.6177
  Y = 3.77373
FEATURE [TechDraw::DrawViewDimension] Dimension039
  AngleOverride = false
  Arbitrary = false
  ArbitraryTolerances = false
  EqualTolerance = true
  ExtensionAngle = 0
  FormatSpec = %.1f
  FormatSpecOverTolerance = %+.1f
  FormatSpecUnderTolerance = %+.1f
  Inverted = false
  LineAngle = 0
  LockPosition = false
  MeasureType = 1
  OverTolerance = 0
  References2D = -> [ProjItem009]
  Rotation = 0
  Scale = 0.2
  ScaleType = 2
  TheoreticalExact = false
  Type = 1
  UnderTolerance = 0
  X = -55.683
  Y = 1.96105
FEATURE [TechDraw::DrawViewDimension] Dimension040
  AngleOverride = false
  Arbitrary = false
  ArbitraryTolerances = false
  EqualTolerance = true
  ExtensionAngle = 0
  FormatSpec = %.1f
  FormatSpecOverTolerance = %+.1f
  FormatSpecUnderTolerance = %+.1f
  Inverted = false
  LineAngle = 0
  LockPosition = false
  MeasureType = 1
  OverTolerance = 0
  References2D = -> [ProjItem009]
  Rotation = 0
  Scale = 0.2
  ScaleType = 2
  TheoreticalExact = false
  Type = 1
  UnderTolerance = 0
  X = -31.8368
  Y = 19.2772
FEATURE [TechDraw::DrawViewDimension] Dimension041
  AngleOverride = false
  Arbitrary = false
  ArbitraryTolerances = false
  EqualTolerance = true
  ExtensionAngle = 0
  FormatSpec = %.1f
  FormatSpecOverTolerance = %+.1f
  FormatSpecUnderTolerance = %+.1f
  Inverted = false
  LineAngle = 0
  LockPosition = false
  MeasureType = 1
  OverTolerance = 0
  References2D = -> [ProjItem009]
  Rotation = 0
  Scale = 0.2
  ScaleType = 2
  TheoreticalExact = false
  Type = 1
  UnderTolerance = 0
  X = -67.8778
  Y = 23.7122
FEATURE [TechDraw::DrawViewDimension] Dimension042
  AngleOverride = false
  Arbitrary = false
  ArbitraryTolerances = false
  EqualTolerance = true
  ExtensionAngle = 0
  FormatSpec = %.1f
  FormatSpecOverTolerance = %+.1f
  FormatSpecUnderTolerance = %+.1f
  Inverted = false
  LineAngle = 0
  LockPosition = false
  MeasureType = 1
  OverTolerance = 0
  References2D = -> [ProjItem009]
  Rotation = 0
  Scale = 0.2
  ScaleType = 2
  TheoreticalExact = false
  Type = 1
  UnderTolerance = 0
  X = -0.404328
  Y = 25.7339
FEATURE [TechDraw::DrawViewDimension] Dimension043
  AngleOverride = false
  Arbitrary = false
  ArbitraryTolerances = false
  EqualTolerance = true
  ExtensionAngle = 0
  FormatSpec = %.1f
  FormatSpecOverTolerance = %+.1f
  FormatSpecUnderTolerance = %+.1f
  Inverted = false
  LineAngle = 0
  LockPosition = false
  MeasureType = 1
  OverTolerance = 0
  References2D = -> [ProjItem011]
  Rotation = 0
  Scale = 0.2
  ScaleType = 2
  TheoreticalExact = false
  Type = 2
  UnderTolerance = 0
  X = -95.0492
  Y = 17.9112
FEATURE [TechDraw::DrawViewDimension] Dimension044
  AngleOverride = false
  Arbitrary = false
  ArbitraryTolerances = false
  EqualTolerance = true
  ExtensionAngle = 0
  FormatSpec = %.1f
  FormatSpecOverTolerance = %+.1f
  FormatSpecUnderTolerance = %+.1f
  Inverted = false
  LineAngle = 0
  LockPosition = false
  MeasureType = 1
  OverTolerance = 0
  References2D = -> [ProjItem010]
  Rotation = 0
  Scale = 0.2
  ScaleType = 2
  TheoreticalExact = false
  Type = 1
  UnderTolerance = 0
  X = 9.80132
  Y = -21.6511
FEATURE [TechDraw::DrawViewDimension] Dimension045
  AngleOverride = false
  Arbitrary = false
  ArbitraryTolerances = false
  EqualTolerance = true
  ExtensionAngle = 0
  FormatSpec = %.1f
  FormatSpecOverTolerance = %+.1f
  FormatSpecUnderTolerance = %+.1f
  Inverted = false
  LineAngle = 0
  LockPosition = false
  MeasureType = 1
  OverTolerance = 0
  References2D = -> [ProjItem011]
  Rotation = 0
  Scale = 0.2
  ScaleType = 2
  TheoreticalExact = false
  Type = 2
  UnderTolerance = 0
  X = 19.0012
  Y = -6.35535
FEATURE [TechDraw::DrawViewDimension] Dimension046
  AngleOverride = false
  Arbitrary = false
  ArbitraryTolerances = false
  EqualTolerance = true
  ExtensionAngle = 0
  FormatSpec = %.1f
  FormatSpecOverTolerance = %+.1f
  FormatSpecUnderTolerance = %+.1f
  Inverted = false
  LineAngle = 0
  LockPosition = false
  MeasureType = 1
  OverTolerance = 0
  References2D = -> [ProjItem011]
  Rotation = 0
  Scale = 0.2
  ScaleType = 2
  TheoreticalExact = false
  Type = 6
  UnderTolerance = 0
  X = 70.9837
  Y = 30.2761
FEATURE [TechDraw::DrawViewDimension] Dimension047
  AngleOverride = false
  Arbitrary = false
  ArbitraryTolerances = false
  EqualTolerance = true
  ExtensionAngle = 0
  FormatSpec = %.1f
  FormatSpecOverTolerance = %+.1f
  FormatSpecUnderTolerance = %+.1f
  Inverted = false
  LineAngle = 0
  LockPosition = false
  MeasureType = 1
  OverTolerance = 0
  References2D = -> [ProjItem011]
  Rotation = 0
  Scale = 0.2
  ScaleType = 2
  TheoreticalExact = false
  Type = 1
  UnderTolerance = 0
  X = -0.0712
  Y = 21.5215
FEATURE [TechDraw::DrawViewDimension] Dimension048
  AngleOverride = false
  Arbitrary = false
  ArbitraryTolerances = false
  EqualTolerance = true
  ExtensionAngle = 0
  FormatSpec = %.1f
  FormatSpecOverTolerance = %+.1f
  FormatSpecUnderTolerance = %+.1f
  Inverted = false
  LineAngle = 0
  LockPosition = false
  MeasureType = 1
  OverTolerance = 0
  References2D = -> [ProjItem011]
  Rotation = 0
  Scale = 0.2
  ScaleType = 2
  TheoreticalExact = false
  Type = 1
  UnderTolerance = 0
  X = -41.1118
  Y = -6.22688
FEATURE [TechDraw::DrawViewBalloon] Balloon003
  BubbleShape = 0
  EndType = 0
  EndTypeScale = 1
  KinkLength = 5
  LockPosition = false
  OriginX = 94.1264
  OriginY = -11.7397
  Rotation = 0
  Scale = 0.2
  ScaleType = 2
  ShapeScale = 1
  SourceView = -> ProjItem010
  Text = 1
  TextWrapLen = -1
  X = 194.126
  Y = 88.2603
FEATURE [TechDraw::DrawViewAnnotation] Annotation003
  Font = Arial
  LineSpace = 80
  LockPosition = false
  MaxWidth = -1
  Rotation = 0
  Scale = 0.2
  ScaleType = 2
  Text = U-65
  TextSize = 5
  TextStyle = 0
  X = 323.588
  Y = 218.927
FEATURE [TechDraw::DrawPage] Page003  label="Page_R406_508_610"
  KeepUpdated = true
  NextBalloonIndex = 2
  ProjectionType = 0
  Template = -> Template003
  Views = -> [ProjGroup003,Dimension033,Dimension034,Dimension035,Dimension036,Dimension037,Dimension038,Dimension039,Dimension040,Dimension041,Dimension042,Dimension043,Dimension044,Dimension045,Dimension046,Dimension047,Dimension048,Balloon003,Annotation003]
FEATURE [Sketcher::SketchObject] Sketch022
  FullyConstrained = true
  sketch-geometry (10):
    g0: Circle CenterX=0 CenterY=0 CenterZ=0 NormalX=0 NormalY=0 NormalZ=1 AngleXU=0 Radius=457
    g1: LineSegment StartX=-244.451 StartY=390.254 StartZ=0 EndX=-30 EndY=490.254 EndZ=0
    g2: LineSegment StartX=30 StartY=490.254 StartZ=0 EndX=244.451 EndY=390.254 EndZ=0
    g3: LineSegment StartX=-30 StartY=490.254 StartZ=0 EndX=30 EndY=490.254 EndZ=0
    g4: LineSegment StartX=244.451 StartY=390.254 StartZ=0 EndX=525 EndY=390.254 EndZ=0
    g5: LineSegment StartX=525 StartY=390.254 StartZ=0 EndX=525 EndY=490.254 EndZ=0
    g6: LineSegment StartX=525 StartY=490.254 StartZ=0 EndX=30 EndY=490.254 EndZ=0
    g7: LineSegment StartX=-30 StartY=490.254 StartZ=0 EndX=-525 EndY=490.254 EndZ=0
    g8: LineSegment StartX=-525 StartY=490.254 StartZ=0 EndX=-525 EndY=390.254 EndZ=0
    g9: LineSegment StartX=-525 StartY=390.254 StartZ=0 EndX=-244.451 EndY=390.254 EndZ=0
  constraints (26):
    c: Coincident(g0,g-1)
    c: Tangent(g1,g0)
    c: Symmetric(g1,g2,g-2)
    c: Symmetric(g1,g2,g-2)
    c: Coincident(g3,g1)
    c: Coincident(g3,g2)
    c: Coincident(g2,g4)
    c: Horizontal(g4)
    c: Coincident(g4,g5)
    c: Vertical(g5)
    c: Coincident(g5,g6)
    c: Coincident(g6,g2)
    c: Horizontal(g6)
    c: Coincident(g1,g7)
    c: Horizontal(g7)
    c: Coincident(g7,g8)
    c: Vertical(g8)
    c: Coincident(g8,g9)
    c: Coincident(g9,g1)
    c: Horizontal(g9)
    c: Equal(g6,g7)
    c: Angle(g-1,g1) = 0.436332
    c: DistanceX(g3,g3) = 60
    c: Diameter(g0) = 914
    c: DistanceY(g5,g5) = 100
    c: DistanceX(g7,g5) = 1050
FEATURE [Part::Cylinder] Cylinder002
  Angle = 360
  AttacherType = Attacher::AttachEngine3D
  FirstAngle = 0
  Height = 600
  Placement = pos=(480,534.254,95) rot=(1,0,0;1.5708rad)
  Radius = 6
  SecondAngle = 0
FEATURE [Part::Extrusion] Extrude020  label="Eckblech009"
  Base = -> Sketch022
  Dir = (0,0,1)
  DirMode = 2
  FaceMakerClass = Part::FaceMakerBullseye
  LengthFwd = 10
  LengthRev = 0
  Solid = true
  Symmetric = false
FEATURE [Part::FeaturePython] Clone007  label="Eckblech008"  # Draft clone (typed FeaturePython)
  AttacherType = Attacher::AttachEngine3D
  Fuse = false
  Objects = -> [Extrude020]
  Placement = pos=(0,0,110) rot=(0,0,1;0rad)
  Scale = (1,1,1)
FEATURE [Sketcher::SketchObject] Sketch025
  ExternalGeometry = -> [Clone007,Extrude020]
  FullyConstrained = true
  MapMode = 5
  Placement = pos=(0,490.254,0) rot=(0,0.707107,0.707107;3.14159rad)
  Support = -> [Extrude020]
  sketch-geometry (4):
    g0: LineSegment StartX=-525 StartY=0 StartZ=0 EndX=525 EndY=0 EndZ=0
    g1: LineSegment StartX=525 StartY=0 StartZ=0 EndX=525 EndY=120 EndZ=0
    g2: LineSegment StartX=525 StartY=120 StartZ=0 EndX=-525 EndY=120 EndZ=0
    g3: LineSegment StartX=-525 StartY=120 StartZ=0 EndX=-525 EndY=0 EndZ=0
  constraints (10):
    c: Coincident(g0,g1)
    c: Coincident(g1,g2)
    c: Coincident(g2,g3)
    c: Coincident(g3,g0)
    c: Horizontal(g0)
    c: Horizontal(g2)
    c: Vertical(g1)
    c: Vertical(g3)
    c: Coincident(g0,g-4)
    c: Coincident(g1,g-3)
FEATURE [Part::Extrusion] Extrude023
  Base = -> Sketch025
  Dir = (0,1,-2e-16)
  DirMode = 2
  FaceMakerClass = Part::FaceMakerBullseye
  LengthFwd = 15
  LengthRev = 0
  Solid = true
  Symmetric = false
FEATURE [Sketcher::SketchObject] Sketch023
  ExternalGeometry = -> [Clone007,Extrude020]
  FullyConstrained = true
  MapMode = 5
  Placement = pos=(0,490.254,0) rot=(1,0,0;1.5708rad)
  Support = -> [Extrude023]
  sketch-geometry (36):
    g0: ArcOfCircle CenterX=-420 CenterY=95 CenterZ=0 NormalX=0 NormalY=0 NormalZ=1 AngleXU=0 Radius=7 StartAngle=1.5708 EndAngle=4.71239
    g1: ArcOfCircle CenterX=-365 CenterY=95 CenterZ=0 NormalX=0 NormalY=0 NormalZ=1 AngleXU=0 Radius=7 StartAngle=4.71239 EndAngle=7.85398
    g2: LineSegment StartX=-420 StartY=88 StartZ=0 EndX=-365 EndY=88 EndZ=0
    g3: LineSegment StartX=-420 StartY=102 StartZ=0 EndX=-365 EndY=102 EndZ=0
    g4: ArcOfCircle CenterX=365 CenterY=95 CenterZ=0 NormalX=0 NormalY=0 NormalZ=1 AngleXU=0 Radius=7 StartAngle=1.5708 EndAngle=4.71239
    g5: ArcOfCircle CenterX=420 CenterY=95 CenterZ=0 NormalX=0 NormalY=0 NormalZ=1 AngleXU=0 Radius=7 StartAngle=4.71239 EndAngle=7.85398
    g6: LineSegment StartX=365 StartY=88 StartZ=0 EndX=420 EndY=88 EndZ=0
    g7: LineSegment StartX=365 StartY=102 StartZ=0 EndX=420 EndY=102 EndZ=0
    g8: ArcOfCircle CenterX=-420 CenterY=25 CenterZ=0 NormalX=0 NormalY=0 NormalZ=1 AngleXU=0 Radius=7 StartAngle=1.5708 EndAngle=4.71239
    g9: ArcOfCircle CenterX=-365 CenterY=25 CenterZ=0 NormalX=0 NormalY=0 NormalZ=1 AngleXU=0 Radius=7 StartAngle=4.71239 EndAngle=7.85398
    g10: LineSegment StartX=-420 StartY=18 StartZ=0 EndX=-365 EndY=18 EndZ=0
    g11: LineSegment StartX=-420 StartY=32 StartZ=0 EndX=-365 EndY=32 EndZ=0
    g12: ArcOfCircle CenterX=365 CenterY=25 CenterZ=0 NormalX=0 NormalY=0 NormalZ=1 AngleXU=0 Radius=7 StartAngle=1.5708 EndAngle=4.71239
    g13: ArcOfCircle CenterX=420 CenterY=25 CenterZ=0 NormalX=0 NormalY=0 NormalZ=1 AngleXU=0 Radius=7 StartAngle=4.71239 EndAngle=7.85398
    g14: LineSegment StartX=365 StartY=18 StartZ=0 EndX=420 EndY=18 EndZ=0
    g15: LineSegment StartX=365 StartY=32 StartZ=0 EndX=420 EndY=32 EndZ=0
    g16: LineSegment StartX=-525 StartY=110 StartZ=0 EndX=-420 EndY=95 EndZ=0
    g17: LineSegment StartX=525 StartY=110 StartZ=0 EndX=420 EndY=95 EndZ=0
    g18: LineSegment StartX=-525 StartY=10 StartZ=0 EndX=-420 EndY=25 EndZ=0
    g19: ArcOfCircle CenterX=-420 CenterY=95 CenterZ=0 NormalX=0 NormalY=0 NormalZ=1 AngleXU=0 Radius=7 StartAngle=2e-16 EndAngle=1.5708
    g20: ArcOfCircle CenterX=-480 CenterY=95 CenterZ=0 NormalX=0 NormalY=0 NormalZ=1 AngleXU=0 Radius=7 StartAngle=1.5708 EndAngle=4.71239
    g21: ArcOfCircle CenterX=-465 CenterY=95 CenterZ=0 NormalX=0 NormalY=0 NormalZ=1 AngleXU=0 Radius=7 StartAngle=4.71239 EndAngle=7.85398
    g22: LineSegment StartX=-480 StartY=88 StartZ=0 EndX=-465 EndY=88 EndZ=0
    g23: LineSegment StartX=-480 StartY=102 StartZ=0 EndX=-465 EndY=102 EndZ=0
    g24: ArcOfCircle CenterX=-480 CenterY=25 CenterZ=0 NormalX=0 NormalY=0 NormalZ=1 AngleXU=0 Radius=7 StartAngle=1.5708 EndAngle=4.71239
    g25: ArcOfCircle CenterX=-465 CenterY=25 CenterZ=0 NormalX=0 NormalY=0 NormalZ=1 AngleXU=0 Radius=7 StartAngle=4.71239 EndAngle=7.85398
    g26: LineSegment StartX=-480 StartY=18 StartZ=0 EndX=-465 EndY=18 EndZ=0
    g27: LineSegment StartX=-480 StartY=32 StartZ=0 EndX=-465 EndY=32 EndZ=0
    g28: ArcOfCircle CenterX=465 CenterY=95 CenterZ=0 NormalX=0 NormalY=0 NormalZ=1 AngleXU=0 Radius=7 StartAngle=1.5708 EndAngle=4.71239
    g29: ArcOfCircle CenterX=480 CenterY=95 CenterZ=0 NormalX=0 NormalY=0 NormalZ=1 AngleXU=0 Radius=7 StartAngle=4.71239 EndAngle=7.85398
    g30: LineSegment StartX=465 StartY=88 StartZ=0 EndX=480 EndY=88 EndZ=0
    g31: LineSegment StartX=465 StartY=102 StartZ=0 EndX=480 EndY=102 EndZ=0
    g32: ArcOfCircle CenterX=465 CenterY=25 CenterZ=0 NormalX=0 NormalY=0 NormalZ=1 AngleXU=0 Radius=7 StartAngle=1.5708 EndAngle=4.71239
    g33: ArcOfCircle CenterX=480 CenterY=25 CenterZ=0 NormalX=0 NormalY=0 NormalZ=1 AngleXU=0 Radius=7 StartAngle=4.71239 EndAngle=7.85398
    g34: LineSegment StartX=465 StartY=18 StartZ=0 EndX=480 EndY=18 EndZ=0
    g35: LineSegment StartX=465 StartY=32 StartZ=0 EndX=480 EndY=32 EndZ=0
  constraints (85):
    c: Tangent(g0,g3) = 1.5708
    c: Tangent(g2,g1) = -1.5708
    c: Tangent(g3,g1) = 1.5708
    c: Equal(g0,g1)
    c: Tangent(g4,g7) = 1.5708
    c: Tangent(g4,g6) = -1.5708
    c: Tangent(g6,g5) = -1.5708
    c: Tangent(g7,g5) = 1.5708
    c: Horizontal(g6)
    c: Equal(g4,g5)
    c: Tangent(g8,g11) = 1.5708
    c: Tangent(g8,g10) = -1.5708
    c: Tangent(g10,g9) = -1.5708
    c: Tangent(g11,g9) = 1.5708
    c: Horizontal(g10)
    c: Equal(g8,g9)
    c: Tangent(g12,g15) = 1.5708
    c: Tangent(g12,g14) = -1.5708
    c: Tangent(g14,g13) = -1.5708
    c: Tangent(g15,g13) = 1.5708
    c: Horizontal(g14)
    c: Equal(g12,g13)
    c: Symmetric(g1,g4,g-2)
    c: Symmetric(g9,g12,g-2)
    c: Vertical(g1,g9)
    c: Equal(g9,g1)
    c: Equal(g1,g4)
    c: Equal(g4,g12)
    c: Equal(g3,g11)
    c: Equal(g11,g7)
    c: Equal(g7,g15)
    c: Diameter(g0) = 14
    c: Coincident(g16,g-4)
    c: Coincident(g16,g0)
    c: Coincident(g17,g-3)
    c: Coincident(g17,g5)
    c: DistanceY(g8,g0) = 70
    c: Tangent(g0,g2) = -1.5708
    c: Horizontal(g2)
    c: Coincident(g18,g-6)
    c: Coincident(g18,g8)
    c: Equal(g16,g18)
    c: Coincident(g19,g0)
    c: Coincident(g19,g0)
    c: Horizontal(g19,g0)
    c: DistanceX(g3,g3) = 55
    c: Tangent(g20,g23) = 1.5708
    c: Tangent(g20,g22) = -1.5708
    c: Tangent(g22,g21) = -1.5708
    c: Tangent(g23,g21) = 1.5708
    c: Horizontal(g22)
    c: Equal(g20,g21)
    c: Tangent(g24,g27) = 1.5708
    c: Tangent(g24,g26) = -1.5708
    c: Tangent(g26,g25) = -1.5708
    c: Tangent(g27,g25) = 1.5708
    c: Horizontal(g26)
    c: Equal(g24,g25)
    c: Tangent(g28,g31) = 1.5708
    c: Tangent(g28,g30) = -1.5708
    c: Tangent(g30,g29) = -1.5708
    c: Tangent(g31,g29) = 1.5708
    c: Horizontal(g30)
    c: Equal(g28,g29)
    c: Tangent(g32,g35) = 1.5708
    c: Tangent(g32,g34) = -1.5708
    c: Tangent(g34,g33) = -1.5708
    c: Tangent(g35,g33) = 1.5708
    c: Horizontal(g34)
    c: Equal(g32,g33)
    c: Equal(g22,g27)
    c: Equal(g27,g30)
    c: Equal(g30,g35)
    c: Equal(g0,g21)
    c: Equal(g21,g25)
    c: Equal(g25,g28)
    c: Equal(g28,g32)
    c: Symmetric(g28,g21,g-2)
    c: Horizontal(g21,g0)
    c: Symmetric(g32,g25,g-2)
    c: Vertical(g21,g25)
    c: DistanceX(g22,g22) = 15
    c: Horizontal(g25,g8)
    c: DistanceX(g13,g32) = 45
    c: DistanceX(g1,g4) = 730
FEATURE [Sketcher::SketchObject] Sketch024
  ExternalGeometry = -> [Extrude023]
  FullyConstrained = true
  MapMode = 5
  Placement = pos=(0,505.254,0) rot=(0,0.707107,0.707107;3.14159rad)
  Support = -> [Extrude023]
  sketch-geometry (13):
    g0: LineSegment StartX=-32.5 StartY=39 StartZ=0 EndX=-32.5 EndY=81 EndZ=0
    g1: LineSegment StartX=-32.5 StartY=81 StartZ=0 EndX=32.5 EndY=81 EndZ=0
    g2: LineSegment StartX=32.5 StartY=81 StartZ=0 EndX=32.5 EndY=39 EndZ=0
    g3: LineSegment StartX=-32.5 StartY=81 StartZ=0 EndX=-525 EndY=120 EndZ=0
    g4: LineSegment StartX=32.5 StartY=81 StartZ=0 EndX=525 EndY=120 EndZ=0
    g5: LineSegment StartX=-16.5 StartY=75.5 StartZ=0 EndX=16.5 EndY=75.5 EndZ=0
    g6: LineSegment StartX=23.89 StartY=69.2796 StartZ=0 EndX=28.5586 EndY=42.3175 EndZ=0
    g7: LineSegment StartX=-23.89 StartY=69.2796 StartZ=0 EndX=-28.5586 EndY=42.3175 EndZ=0
    g8: ArcOfCircle CenterX=32.5 CenterY=43 CenterZ=0 NormalX=0 NormalY=0 NormalZ=1 AngleXU=0 Radius=4 StartAngle=3.31305 EndAngle=4.71239
    g9: ArcOfCircle CenterX=16.5 CenterY=68 CenterZ=0 NormalX=0 NormalY=0 NormalZ=1 AngleXU=0 Radius=7.5 StartAngle=0.171455 EndAngle=1.5708
    g10: ArcOfCircle CenterX=-32.5 CenterY=43 CenterZ=0 NormalX=0 NormalY=0 NormalZ=1 AngleXU=0 Radius=4 StartAngle=4.71239 EndAngle=6.11173
    g11: ArcOfCircle CenterX=-16.5 CenterY=68 CenterZ=0 NormalX=0 NormalY=0 NormalZ=1 AngleXU=0 Radius=7.5 StartAngle=1.5708 EndAngle=2.97014
    g12: LineSegment StartX=-525 StartY=0 StartZ=0 EndX=-32.5 EndY=39 EndZ=0
  constraints (35):
    c: Vertical(g0)
    c: Coincident(g0,g1)
    c: Horizontal(g1)
    c: Coincident(g1,g2)
    c: Vertical(g2)
    c: Coincident(g3,g0)
    c: Coincident(g4,g1)
    c: Coincident(g3,g-4)
    c: Coincident(g4,g-3)
    c: Equal(g3,g4)
    c: DistanceX(g1,g1) = 65
    c: DistanceY(g0,g0) = 42
    c: Equal(g0,g2)
    c: PointOnObject(g8,g2)
    c: Coincident(g8,g2)
    c: Coincident(g9,g5)
    c: Vertical(g9,g5)
    c: Tangent(g6,g9) = 1.5708
    c: Tangent(g8,g6) = -1.5708
    c: Symmetric(g5,g5,g-2)
    c: DistanceY(g5,g1) = 5.5
    c: Radius(g9) = 7.5
    c: Radius(g8) = 4
    c: DistanceX(g5,g5) = 33
    c: PointOnObject(g10,g0)
    c: Coincident(g10,g0)
    c: Coincident(g11,g5)
    c: Vertical(g11,g5)
    c: Equal(g9,g11)
    c: Tangent(g11,g7) = -1.5708
    c: Equal(g8,g10)
    c: Tangent(g10,g7) = 1.5708
    c: Coincident(g12,g-4)
    c: Coincident(g12,g0)
    c: Equal(g3,g12)
FEATURE [Part::Extrusion] Extrude022
  Base = -> Sketch024
  Dir = (0,1,-2e-16)
  DirMode = 2
  FaceMakerClass = Part::FaceMakerBullseye
  LengthFwd = 135
  LengthRev = 0
  Solid = true
  Symmetric = false
FEATURE [Sketcher::SketchObject] Sketch021
  ExternalGeometry = -> [Extrude022]
  FullyConstrained = true
  MapMode = 5
  Placement = pos=(0,1.78e-14,81) rot=(0,0,1;0rad)
  Support = -> [Extrude022]
  sketch-geometry (7):
    g0: LineSegment StartX=-10 StartY=620.254 StartZ=0 EndX=10 EndY=620.254 EndZ=0
    g1: LineSegment StartX=10 StartY=620.254 StartZ=0 EndX=10 EndY=600.254 EndZ=0
    g2: LineSegment StartX=10 StartY=600.254 StartZ=0 EndX=-10 EndY=600.254 EndZ=0
    g3: LineSegment StartX=-10 StartY=600.254 StartZ=0 EndX=-10 EndY=620.254 EndZ=0
    g4: LineSegment StartX=-10 StartY=620.254 StartZ=0 EndX=-32.5 EndY=640.254 EndZ=0
    g5: LineSegment StartX=10 StartY=620.254 StartZ=0 EndX=32.5 EndY=640.254 EndZ=0
    g6: LineSegment StartX=10 StartY=610.254 StartZ=0 EndX=32.5 EndY=610.254 EndZ=0
  constraints (19):
    c: Coincident(g0,g1)
    c: Coincident(g1,g2)
    c: Coincident(g2,g3)
    c: Coincident(g3,g0)
    c: Horizontal(g0)
    c: Horizontal(g2)
    c: Vertical(g1)
    c: Vertical(g3)
    c: DistanceX(g2,g2) = 20
    c: DistanceY(g1,g1) = 20
    c: Coincident(g4,g0)
    c: Coincident(g5,g0)
    c: Coincident(g4,g-3)
    c: Coincident(g5,g-3)
    c: Equal(g4,g5)
    c: PointOnObject(g6,g1)
    c: Vertical(g5,g6)
    c: Symmetric(g1,g0,g6)
    c: DistanceY(g6,g5) = 30
FEATURE [Part::Extrusion] Extrude021
  Base = -> Sketch021
  Dir = (0,2e-16,1)
  DirMode = 2
  FaceMakerClass = Part::FaceMakerBullseye
  LengthFwd = 30
  LengthRev = 0
  Solid = true
  Symmetric = true
FEATURE [Part::Cut] Cut008  label="U070"
  Base = -> Extrude022
  Refine = true
  Tool = -> Extrude021
FEATURE [Part::Extrusion] Extrude024
  Base = -> Sketch023
  Dir = (0,1,0)
  DirMode = 0
  FaceMakerClass = Part::FaceMakerBullseye
  LengthFwd = 50
  LengthRev = 0
  Solid = true
  Symmetric = true
FEATURE [Part::Cut] Cut009
  Base = -> Extrude023
  Refine = true
  Tool = -> Extrude024
FEATURE [Part::FeaturePython] BooleanFragments005  label="BooleanFragments006"  # WARN: FeaturePython — macro-defined, semantics opaque (R4)
  Mode = 0
  Objects = -> [Extrude020,Clone007,Cut009]
  Tolerance = 0
FEATURE [Part::Feature] BOLTS_part010  label="Circular hollow profile 711.0/10.0 l=360.0"
  Placement = pos=(0,0,-120) rot=(0,0,1;0rad)
  shape: bbox 711 x 711 x 360 mm, 4 faces (baked)
FEATURE [Part::Feature] BOLTS_part011  label="Circular hollow profile 762.0/10.0 l=360.0"
  Placement = pos=(0,0,-120) rot=(0,0,1;0rad)
  shape: bbox 762 x 762 x 360 mm, 4 faces (baked)
FEATURE [Part::Feature] BOLTS_part012  label="Circular hollow profile 813.0/10.0 l=360.0"
  Placement = pos=(0,0,-120) rot=(0,0,1;0rad)
  shape: bbox 813 x 813 x 360 mm, 4 faces (baked)
FEATURE [App::DocumentObjectGroup] Group  label="R711_762_813_914"
  Group = -> [BOLTS_part008,Cylinder002,BooleanFragments005,BOLTS_part010,BOLTS_part011,BOLTS_part012,Cut008]
FEATURE [TechDraw::DrawSVGTemplate] Template004
  EditableTexts = AUTHOR_NAME=Axians,DN=DN,DRAWING_TITLE=Leiterhalterung,FC-DATE=07.05.2021,FC-REV=REV A,FC-SC=1:5,FC-SH=X / Y,FC-SI=A3,+6 more (map truncated)
  Height = 297
  Orientation = 1
  Width = 420
FEATURE [TechDraw::DrawProjGroupItem] ProjItem012  label="Front004"
  CoarseView = false
  Direction = (0,1,0)
  Focus = 100
  HardHidden = true
  IsoCount = 0
  IsoHidden = false
  IsoVisible = false
  LockPosition = true
  Perspective = false
  Rotation = 0
  RotationVector = (-1,0,0)
  Scale = 0.2
  ScaleType = 2
  ScrubCount = 0
  SeamHidden = false
  SeamVisible = true
  SmoothHidden = false
  SmoothVisible = true
  Source = -> [BooleanFragments005,Cut008]
  Type = 0
  X = 0
  XDirection = (-1,0,0)
  Y = 0
FEATURE [TechDraw::DrawProjGroupItem] ProjItem013  label="Left004"
  CoarseView = false
  Direction = (1,1e-16,0)
  Focus = 100
  HardHidden = true
  IsoCount = 0
  IsoHidden = false
  IsoVisible = false
  LockPosition = false
  Perspective = false
  Rotation = 0
  RotationVector = (1,0,0)
  Scale = 0.2
  ScaleType = 2
  ScrubCount = 0
  SeamHidden = false
  SeamVisible = true
  SmoothHidden = false
  SmoothVisible = true
  Source = -> [BooleanFragments005,Cut008]
  Type = 1
  X = 145
  XDirection = (-1e-16,1,0)
  Y = 0
FEATURE [TechDraw::DrawProjGroupItem] ProjItem014  label="Top004"
  CoarseView = false
  Direction = (0,0,1)
  Focus = 100
  HardHidden = true
  IsoCount = 0
  IsoHidden = false
  IsoVisible = false
  LockPosition = false
  Perspective = false
  Rotation = 0
  RotationVector = (1,0,0)
  Scale = 0.2
  ScaleType = 2
  ScrubCount = 0
  SeamHidden = false
  SeamVisible = true
  SmoothHidden = false
  SmoothVisible = true
  Source = -> [BooleanFragments005,Cut008]
  Type = 4
  X = 0
  XDirection = (-1,0,0)
  Y = -52
FEATURE [TechDraw::DrawProjGroup] ProjGroup004
  Anchor = -> ProjItem012
  AutoDistribute = true
  LockPosition = false
  ProjectionType = 0
  Rotation = 0
  Scale = 0.2
  ScaleType = 2
  Source = -> [BooleanFragments005,Cut008]
  Views = -> [ProjItem012,ProjItem013,ProjItem014]
  X = 151.244
  Y = 237.037
  spacingX = 15
  spacingY = 15
FEATURE [TechDraw::DrawViewBalloon] Balloon004
  BubbleShape = 0
  EndType = 0
  EndTypeScale = 1
  KinkLength = 5
  LockPosition = false
  OriginX = 100.366
  OriginY = -6.03659
  Rotation = 0
  Scale = 0.2
  ScaleType = 2
  ShapeScale = 1
  SourceView = -> ProjItem013
  Text = 1
  TextWrapLen = -1
  X = 200.366
  Y = 93.9634
FEATURE [TechDraw::DrawViewAnnotation] Annotation004
  Font = Arial
  LineSpace = 80
  LockPosition = false
  MaxWidth = -1
  Rotation = 0
  Scale = 0.2
  ScaleType = 2
  Text = U-65
  TextSize = 5
  TextStyle = 0
  X = 371.78
  Y = 254.744
FEATURE [TechDraw::DrawViewDimension] Dimension049
  AngleOverride = false
  Arbitrary = false
  ArbitraryTolerances = false
  EqualTolerance = true
  ExtensionAngle = 0
  FormatSpec = %.1f
  FormatSpecOverTolerance = %+.1f
  FormatSpecUnderTolerance = %+.1f
  Inverted = false
  LineAngle = 0
  LockPosition = false
  MeasureType = 1
  OverTolerance = 0
  References2D = -> [ProjItem012]
  Rotation = 0
  Scale = 0.2
  ScaleType = 2
  TheoreticalExact = false
  Type = 1
  UnderTolerance = 0
  X = 0.425202
  Y = 26.6695
FEATURE [TechDraw::DrawViewDimension] Dimension050
  AngleOverride = false
  Arbitrary = false
  ArbitraryTolerances = false
  EqualTolerance = true
  ExtensionAngle = 0
  FormatSpec = %.1f
  FormatSpecOverTolerance = %+.1f
  FormatSpecUnderTolerance = %+.1f
  Inverted = false
  LineAngle = 0
  LockPosition = false
  MeasureType = 1
  OverTolerance = 0
  References2D = -> [ProjItem012]
  Rotation = 0
  Scale = 0.2
  ScaleType = 2
  TheoreticalExact = false
  Type = 2
  UnderTolerance = 0
  X = -120.945
  Y = 0
FEATURE [TechDraw::DrawViewDimension] Dimension051
  AngleOverride = false
  Arbitrary = false
  ArbitraryTolerances = false
  EqualTolerance = true
  ExtensionAngle = 0
  FormatSpec = %.1f
  FormatSpecOverTolerance = %+.1f
  FormatSpecUnderTolerance = %+.1f
  Inverted = false
  LineAngle = 0
  LockPosition = false
  MeasureType = 1
  OverTolerance = 0
  References2D = -> [ProjItem014]
  Rotation = 0
  Scale = 0.2
  ScaleType = 2
  TheoreticalExact = false
  Type = 2
  UnderTolerance = 0
  X = -117.118
  Y = 14.5748
FEATURE [TechDraw::DrawViewDimension] Dimension052
  AngleOverride = false
  Arbitrary = false
  ArbitraryTolerances = false
  EqualTolerance = true
  ExtensionAngle = 0
  FormatSpec = %.1f
  FormatSpecOverTolerance = %+.1f
  FormatSpecUnderTolerance = %+.1f
  Inverted = false
  LineAngle = 0
  LockPosition = false
  MeasureType = 1
  OverTolerance = 0
  References2D = -> [ProjItem013]
  Rotation = 0
  Scale = 0.2
  ScaleType = 2
  TheoreticalExact = false
  Type = 2
  UnderTolerance = 0
  X = -36.2313
  Y = 18.9742
FEATURE [TechDraw::DrawViewDimension] Dimension053
  AngleOverride = false
  Arbitrary = false
  ArbitraryTolerances = false
  EqualTolerance = true
  ExtensionAngle = 0
  FormatSpec = %.1f
  FormatSpecOverTolerance = %+.1f
  FormatSpecUnderTolerance = %+.1f
  Inverted = false
  LineAngle = 0
  LockPosition = false
  MeasureType = 1
  OverTolerance = 0
  References2D = -> [ProjItem013]
  Rotation = 0
  Scale = 0.2
  ScaleType = 2
  TheoreticalExact = false
  Type = 1
  UnderTolerance = 0
  X = -17.0899
  Y = 18.1772
FEATURE [TechDraw::DrawViewDimension] Dimension054
  AngleOverride = false
  Arbitrary = false
  ArbitraryTolerances = false
  EqualTolerance = true
  ExtensionAngle = 0
  FormatSpec = %.1f
  FormatSpecOverTolerance = %+.1f
  FormatSpecUnderTolerance = %+.1f
  Inverted = false
  LineAngle = 0
  LockPosition = false
  MeasureType = 1
  OverTolerance = 0
  References2D = -> [ProjItem013]
  Rotation = 0
  Scale = 0.2
  ScaleType = 2
  TheoreticalExact = false
  Type = 1
  UnderTolerance = 0
  X = 11.8882
  Y = -25.1604
FEATURE [TechDraw::DrawViewDimension] Dimension055
  AngleOverride = false
  Arbitrary = false
  ArbitraryTolerances = false
  EqualTolerance = true
  ExtensionAngle = 0
  FormatSpec = %.1f
  FormatSpecOverTolerance = %+.1f
  FormatSpecUnderTolerance = %+.1f
  Inverted = false
  LineAngle = 0
  LockPosition = false
  MeasureType = 1
  OverTolerance = 0
  References2D = -> [ProjItem014]
  Rotation = 0
  Scale = 0.2
  ScaleType = 2
  TheoreticalExact = false
  Type = 2
  UnderTolerance = 0
  X = 15.6941
  Y = -33.5325
FEATURE [TechDraw::DrawViewDimension] Dimension056
  AngleOverride = false
  Arbitrary = false
  ArbitraryTolerances = false
  EqualTolerance = true
  ExtensionAngle = 0
  FormatSpec = %.1f
  FormatSpecOverTolerance = %+.1f
  FormatSpecUnderTolerance = %+.1f
  Inverted = false
  LineAngle = 0
  LockPosition = false
  MeasureType = 1
  OverTolerance = 0
  References2D = -> [ProjItem014]
  Rotation = 0
  Scale = 0.2
  ScaleType = 2
  TheoreticalExact = false
  Type = 6
  UnderTolerance = 0
  X = 88.6835
  Y = 32.9776
FEATURE [TechDraw::DrawViewDimension] Dimension057
  AngleOverride = false
  Arbitrary = false
  ArbitraryTolerances = false
  EqualTolerance = true
  ExtensionAngle = 0
  FormatSpec = %.1f
  FormatSpecOverTolerance = %+.1f
  FormatSpecUnderTolerance = %+.1f
  Inverted = false
  LineAngle = 0
  LockPosition = false
  MeasureType = 1
  OverTolerance = 0
  References2D = -> [ProjItem014]
  Rotation = 0
  Scale = 0.2
  ScaleType = 2
  TheoreticalExact = false
  Type = 1
  UnderTolerance = 0
  X = -0.259985
  Y = 22.9389
FEATURE [TechDraw::DrawViewDimension] Dimension058
  AngleOverride = false
  Arbitrary = false
  ArbitraryTolerances = false
  EqualTolerance = true
  ExtensionAngle = 0
  FormatSpec = %.1f
  FormatSpecOverTolerance = %+.1f
  FormatSpecUnderTolerance = %+.1f
  Inverted = false
  LineAngle = 0
  LockPosition = false
  MeasureType = 1
  OverTolerance = 0
  References2D = -> [ProjItem014]
  Rotation = 0
  Scale = 0.2
  ScaleType = 2
  TheoreticalExact = false
  Type = 1
  UnderTolerance = 0
  X = -56.0589
  Y = -10.9299
FEATURE [TechDraw::DrawViewDimension] Dimension059
  AngleOverride = false
  Arbitrary = false
  ArbitraryTolerances = false
  EqualTolerance = true
  ExtensionAngle = 0
  FormatSpec = %.1f
  FormatSpecOverTolerance = %+.1f
  FormatSpecUnderTolerance = %+.1f
  Inverted = false
  LineAngle = 0
  LockPosition = false
  MeasureType = 1
  OverTolerance = 0
  References2D = -> [ProjItem012]
  Rotation = 0
  Scale = 0.2
  ScaleType = 2
  TheoreticalExact = false
  Type = 1
  UnderTolerance = 0
  X = -88.2047
  Y = 20.5829
FEATURE [TechDraw::DrawViewDimension] Dimension060
  AngleOverride = false
  Arbitrary = false
  ArbitraryTolerances = false
  EqualTolerance = true
  ExtensionAngle = 0
  FormatSpec = %.1f
  FormatSpecOverTolerance = %+.1f
  FormatSpecUnderTolerance = %+.1f
  Inverted = false
  LineAngle = 0
  LockPosition = false
  MeasureType = 1
  OverTolerance = 0
  References2D = -> [ProjItem012]
  Rotation = 0
  Scale = 0.2
  ScaleType = 2
  TheoreticalExact = false
  Type = 1
  UnderTolerance = 0
  X = -0.708671
  Y = 20.6419
FEATURE [TechDraw::DrawViewDimension] Dimension061
  AngleOverride = false
  Arbitrary = false
  ArbitraryTolerances = false
  EqualTolerance = true
  ExtensionAngle = 0
  FormatSpec = %.1f
  FormatSpecOverTolerance = %+.1f
  FormatSpecUnderTolerance = %+.1f
  Inverted = false
  LineAngle = 0
  LockPosition = false
  MeasureType = 1
  OverTolerance = 0
  References2D = -> [ProjItem012]
  Rotation = 0
  Scale = 0.2
  ScaleType = 2
  TheoreticalExact = false
  Type = 1
  UnderTolerance = 0
  X = 84.7558
  Y = 3.11965
FEATURE [TechDraw::DrawViewDimension] Dimension062
  AngleOverride = false
  Arbitrary = false
  ArbitraryTolerances = false
  EqualTolerance = true
  ExtensionAngle = 0
  FormatSpec = %.1f
  FormatSpecOverTolerance = %+.1f
  FormatSpecUnderTolerance = %+.1f
  Inverted = false
  LineAngle = 0
  LockPosition = false
  MeasureType = 1
  OverTolerance = 0
  References2D = -> [ProjItem012]
  Rotation = 0
  Scale = 0.2
  ScaleType = 2
  TheoreticalExact = false
  Type = 1
  UnderTolerance = 0
  X = 61.6691
  Y = 0.600869
FEATURE [TechDraw::DrawViewDimension] Dimension063
  AngleOverride = false
  Arbitrary = false
  ArbitraryTolerances = false
  EqualTolerance = true
  ExtensionAngle = 0
  FormatSpec = %.1f
  FormatSpecOverTolerance = %+.1f
  FormatSpecUnderTolerance = %+.1f
  Inverted = false
  LineAngle = 0
  LockPosition = false
  MeasureType = 1
  OverTolerance = 0
  References2D = -> [ProjItem012]
  Rotation = 0
  Scale = 0.2
  ScaleType = 2
  TheoreticalExact = false
  Type = 2
  UnderTolerance = 0
  X = -101.669
  Y = 0.708671
FEATURE [TechDraw::DrawViewDimension] Dimension064
  AngleOverride = false
  Arbitrary = false
  ArbitraryTolerances = false
  EqualTolerance = true
  ExtensionAngle = 0
  FormatSpec = ⌀%.1f
  FormatSpecOverTolerance = %+.1f
  FormatSpecUnderTolerance = %+.1f
  Inverted = false
  LineAngle = 0
  LockPosition = false
  MeasureType = 1
  OverTolerance = 0
  References2D = -> [ProjItem012]
  Rotation = 0
  Scale = 0.2
  ScaleType = 2
  TheoreticalExact = false
  Type = 5
  UnderTolerance = 0
  X = -61.1228
  Y = -0.708671
FEATURE [TechDraw::DrawPage] Page004
  KeepUpdated = true
  NextBalloonIndex = 2
  ProjectionType = 0
  Template = -> Template004
  Views = -> [ProjGroup004,Balloon004,Annotation004,Dimension049,Dimension050,Dimension051,Dimension052,Dimension053,Dimension054,Dimension055,Dimension056,Dimension057,Dimension058,Dimension059,Dimension060,Dimension061,Dimension062,Dimension063,Dimension064]
FEATURE [Part::Feature] BOLTS_part013  label="Circular hollow profile 139.7/6.3 l=360.001"
  Placement = pos=(0,49,-120) rot=(0,0,1;0rad)
  shape: bbox 139.7 x 139.7 x 360 mm, 4 faces (baked)
FEATURE [Part::FeaturePython] Clone008  label="U071"  # Draft clone (typed FeaturePython)
  AttacherType = Attacher::AttachEngine3D
  Fuse = false
  Objects = -> [Cut002]
  Scale = (1,1,1)
FEATURE [Part::FeaturePython] Clone009  label="Eckblech010"  # Draft clone (typed FeaturePython)
  AttacherType = Attacher::AttachEngine3D
  Fuse = false
  Objects = -> [Extrude005]
  Scale = (1,1,1)
FEATURE [Part::FeaturePython] Clone010  label="Eckblech011"  # Draft clone (typed FeaturePython)
  AttacherType = Attacher::AttachEngine3D
  Fuse = false
  Objects = -> [Clone004]
  Placement = pos=(0,0,110) rot=(0,0,1;0rad)
  Scale = (1,1,1)
FEATURE [Part::FeaturePython] Clone011  label="Cut010"  # Draft clone (typed FeaturePython)
  AttacherType = Attacher::AttachEngine3D
  Fuse = false
  Objects = -> [Cut003]
  Scale = (1,1,1)
FEATURE [Part::Cut] Cut010  label="Cut011"
  Base = -> Clone009
  Refine = true
  Tool = -> BOLTS_part013
FEATURE [Part::Cut] Cut011  label="Cut012"
  Base = -> Clone010
  Refine = true
  Tool = -> BOLTS_part013
FEATURE [Part::MultiFuse] Fusion
  Refine = true
  Shapes = -> [Clone008,Clone011,Cut010,Cut011]
FEATURE [Fem::FemMeshObjectPython] FEMMeshGmsh  # FEM object (typed FeaturePython)
  Algorithm2D = 0
  Algorithm3D = 0
  CharacteristicLengthMax = 5
  CharacteristicLengthMin = 0
  CoherenceMesh = true
  ElementDimension = 3
  ElementOrder = 1
  GeometryTolerance = 1e-06
  GroupsOfNodes = false
  HighOrderOptimize = 0
  MeshSizeFromCurvature = 12
  OptimizeNetgen = false
  OptimizeStd = true
  Part = -> Fusion
  RecombinationAlgorithm = 0
  Recombine3DAll = false
  RecombineAll = false
  SecondOrderLinear = false
FEATURE [Fem::FemSolverObjectPython] SolverCcxTools  # FEM object (typed FeaturePython)
  AnalysisType = 0
  BeamShellResultOutput3D = true
  BucklingFactors = 1
  EigenmodeHighLimit = 1000000
  EigenmodeLowLimit = 0
  EigenmodesCount = 10
  GeometricalNonlinearity = 0
  IterationsControlParameterCutb = 0.25,0.5,0.75,0.85,,,1.5,
  IterationsControlParameterIter = 4,8,9,200,10,400,,200,,
  IterationsControlParameterTimeUse = false
  IterationsThermoMechMaximum = 2000
  IterationsUserDefinedIncrementations = false
  IterationsUserDefinedTimeStepLength = false
  MaterialNonlinearity = 0
  MatrixSolverType = 0
  SplitInputWriter = true
  ThermoMechSteadyState = true
  TimeEnd = 1
  TimeInitialStep = 0.01
FEATURE [App::MaterialObjectPython] MaterialSolid  label="S355"  # material (typed FeaturePython)
  Category = 0
  Material = AuthorAndLicense=(c) 2013 Juergen Riegel (CC-BY 3.0),CardName=CalculiX-Steel,Density=7900 kg/m^3,+8 more (map truncated)
FEATURE [Fem::ConstraintFixed] ConstraintFixed
  NormalDirection = (0.573576,-0.819152,0)
  Normals = (36) [(0.478338,-0.878176,0),(0.573576,-0.819152,0),(0.661614,-0.749845,0),(0.478338,-0.878176,0),(0.573576,-0.819152,0),(0.661614,-0.749845,0),+30 more]
  Points = (36) [(-33.4119,110.341,120),(-40.0643,106.218,120),(-46.2137,101.377,120),(-33.4119,110.341,115),(-40.0643,106.218,115),(-46.2137,101.377,115),+30 more]
  References = -> [Fusion]
FEATURE [Fem::ConstraintForce] ConstraintForce
  Direction = -> Fusion [Edge109]
  DirectionVector = (0,0,-1)
  Force = 6000
  NormalDirection = (1,0,0)
  Points = (36) [(-10,241.482,75.5),(-10,231.482,75.5),(-10,221.482,75.5),(-10,241.482,78.25),(-10,231.482,78.25),(-10,221.482,78.25),(-10,241.482,81),+29 more]
  References = -> [Fusion]
  Reversed = true
FEATURE [Fem::ConstraintForce] ConstraintForce001
  Direction = -> Fusion [Edge102]
  DirectionVector = (0,-1,2e-16)
  Force = 20000
  NormalDirection = (-1,0,2e-16)
  Points = (18) [(120,136.482,68),(127,136.482,75),(120,136.482,82),(120,128.982,68),(127,128.982,75),(120,128.982,82),(120,121.482,68),(127,121.482,75),+10 more]
  References = -> [Fusion]
  Reversed = true
FEATURE [Fem::FemAnalysis] Analysis
  Group = -> [SolverCcxTools,MaterialSolid,ConstraintFixed,ConstraintForce,ConstraintForce001,FEMMeshGmsh]
FEATURE [Part::Feature] Part__Feature  label="leiter"
  Placement = pos=(-6e-14,271,-478) rot=(0,0,1;1.5708rad)
  shape: bbox 382 x 52 x 1200 mm, 62 faces (baked)
